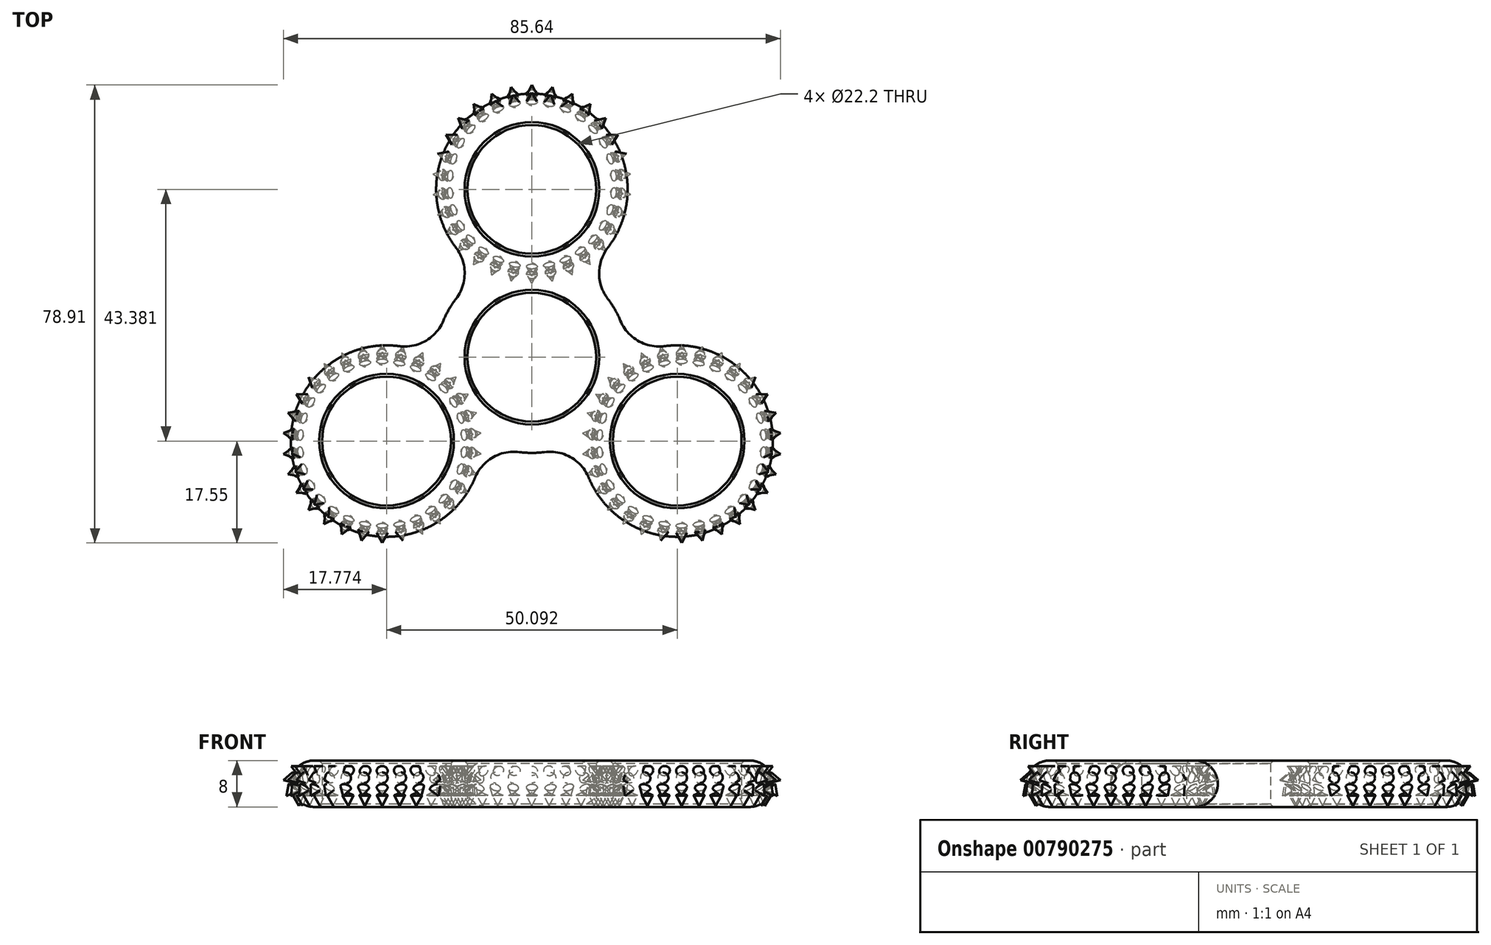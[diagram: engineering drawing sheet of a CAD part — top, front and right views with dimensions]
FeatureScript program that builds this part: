
annotation { "Feature Type Name" : "Feature", "Feature Type Description" : "" }
export const myFeature = defineFeature(function(context is Context, id is Id, definition is map)
    precondition{}
    {
        {
            var Q0;
            Q0=qCreatedBy(makeId("Top.planeOp"),FACE);
            var sketch = newSketch(context, id + "F0", { "sketchPlane" : qUnion([Q0])});
            skCircle(sketch, "E0", {"center": v(0, 0) * mm, "radius": 11.1 * mm});
            skCircle(sketch, "E1", {"center": v(0, 0) * mm, "radius": 16.5 * mm});
            skCircle(sketch, "E2", {"center": v(0, 28.92) * mm, "radius": 16.5 * mm});
            skCircle(sketch, "E3", {"center": v(0, 28.92) * mm, "radius": 11.1 * mm});
            skCircle(sketch, "E4.1.0", {"center": v(-25.05, -14.46) * mm, "radius": 16.5 * mm});
            skCircle(sketch, "E4.1.1", {"center": v(-25.05, -14.46) * mm, "radius": 11.1 * mm});
            skCircle(sketch, "E4.2.0", {"center": v(25.05, -14.46) * mm, "radius": 16.5 * mm});
            skCircle(sketch, "E4.2.1", {"center": v(25.05, -14.46) * mm, "radius": 11.1 * mm});
            skSolve(sketch);
        }
        {
            var Q0;
            Q0=makeQuery(id+"F0.imprint","IMPRINT",FACE,{"disambiguationData":[TD([[makeQuery(id+"F0.imprint","IMPRINT",EDGE,{"derivedFrom":sQuery(id+"F0.wireOp",EDGE,"E4.1.1")}),-1.0]])]});
            var Q1;
            Q1=makeQuery(id+"F0.imprint","IMPRINT",FACE,{"disambiguationData":[TD([[makeQuery(id+"F0.imprint","IMPRINT",EDGE,{"derivedFrom":sQuery(id+"F0.wireOp",EDGE,"E0")}),-1.0]])]});
            var Q2;
            Q2=makeQuery(id+"F0.imprint","IMPRINT",FACE,{"disambiguationData":[TD([[makeQuery(id+"F0.imprint","IMPRINT",EDGE,{"derivedFrom":sQuery(id+"F0.wireOp",EDGE,"E3")}),-1.0]])]});
            var Q3;
            {var subQ0=sQuery(id+"F0.wireOp",EDGE,"E2");var subQ1=sQuery(id+"F0.wireOp",EDGE,"E1");var subQ2=makeQuery(id+"F0.imprint","INTERSECT",VERTEX,{"disambiguationData":[OD(0.0)],"derivedFrom":[subQ1,subQ0]});Q3=makeQuery(id+"F0.imprint","IMPRINT",FACE,{"disambiguationData":[TD([[makeQuery(id+"F0.imprint","IMPRINT",EDGE,{"disambiguationData":[TD([[subQ2,1.0]])],"derivedFrom":subQ1}),1.0]])]});}
            var Q4;
            {var subQ0=sQuery(id+"F0.wireOp",EDGE,"E4.1.0");var subQ1=sQuery(id+"F0.wireOp",EDGE,"E1");var subQ2=makeQuery(id+"F0.imprint","INTERSECT",VERTEX,{"disambiguationData":[OD(0.0)],"derivedFrom":[subQ1,subQ0]});Q4=makeQuery(id+"F0.imprint","IMPRINT",FACE,{"disambiguationData":[TD([[makeQuery(id+"F0.imprint","IMPRINT",EDGE,{"disambiguationData":[TD([[subQ2,-1.0]])],"derivedFrom":subQ1}),1.0]])]});}
            var Q5;
            {var subQ0=sQuery(id+"F0.wireOp",EDGE,"E4.2.0");var subQ1=sQuery(id+"F0.wireOp",EDGE,"E1");var subQ2=makeQuery(id+"F0.imprint","INTERSECT",VERTEX,{"disambiguationData":[OD(0.0)],"derivedFrom":[subQ1,subQ0]});Q5=makeQuery(id+"F0.imprint","IMPRINT",FACE,{"disambiguationData":[TD([[makeQuery(id+"F0.imprint","IMPRINT",EDGE,{"disambiguationData":[TD([[subQ2,-1.0]])],"derivedFrom":subQ1}),1.0]])]});}
            var Q6;
            Q6=makeQuery(id+"F0.imprint","IMPRINT",FACE,{"disambiguationData":[TD([[makeQuery(id+"F0.imprint","IMPRINT",EDGE,{"derivedFrom":sQuery(id+"F0.wireOp",EDGE,"E4.2.1")}),-1.0]])]});
            extrude(context, id + "F1", {"entities" : qUnion([Q0, Q1, Q2, Q3, Q4, Q5, Q6]), "depth" : 8 * mm, "offsetDistance" : 25 * mm});
        }
        {
            var Q0;
            {var subQ0=sQuery(id+"F0.wireOp",EDGE,"E2");var subQ1=sQuery(id+"F0.wireOp",EDGE,"E1");Q0=makeQuery(id+"F1.opExtrude","SWEPT_EDGE",EDGE,{"disambiguationData":[OSD([subQ1,subQ0]),TDD([makeQuery(id+"F0.imprint","INTERSECT",VERTEX,{"disambiguationData":[OD(0.0)],"derivedFrom":[subQ1,subQ0]})])]});}
            var Q1;
            {var subQ0=sQuery(id+"F0.wireOp",EDGE,"E4.1.0");var subQ1=sQuery(id+"F0.wireOp",EDGE,"E1");Q1=makeQuery(id+"F1.opExtrude","SWEPT_EDGE",EDGE,{"disambiguationData":[OSD([subQ1,subQ0]),TDD([makeQuery(id+"F0.imprint","INTERSECT",VERTEX,{"disambiguationData":[OD(0.0)],"derivedFrom":[subQ1,subQ0]})])]});}
            var Q2;
            {var subQ0=sQuery(id+"F0.wireOp",EDGE,"E4.1.0");var subQ1=sQuery(id+"F0.wireOp",EDGE,"E1");Q2=makeQuery(id+"F1.opExtrude","SWEPT_EDGE",EDGE,{"disambiguationData":[OSD([subQ1,subQ0]),TDD([makeQuery(id+"F0.imprint","INTERSECT",VERTEX,{"disambiguationData":[OD(1.0)],"derivedFrom":[subQ1,subQ0]})])]});}
            var Q3;
            {var subQ0=sQuery(id+"F0.wireOp",EDGE,"E4.2.0");var subQ1=sQuery(id+"F0.wireOp",EDGE,"E1");Q3=makeQuery(id+"F1.opExtrude","SWEPT_EDGE",EDGE,{"disambiguationData":[OSD([subQ1,subQ0]),TDD([makeQuery(id+"F0.imprint","INTERSECT",VERTEX,{"disambiguationData":[OD(0.0)],"derivedFrom":[subQ1,subQ0]})])]});}
            var Q4;
            {var subQ0=sQuery(id+"F0.wireOp",EDGE,"E2");var subQ1=sQuery(id+"F0.wireOp",EDGE,"E1");Q4=makeQuery(id+"F1.opExtrude","SWEPT_EDGE",EDGE,{"disambiguationData":[OSD([subQ1,subQ0]),TDD([makeQuery(id+"F0.imprint","INTERSECT",VERTEX,{"disambiguationData":[OD(1.0)],"derivedFrom":[subQ1,subQ0]})])]});}
            var Q5;
            {var subQ0=sQuery(id+"F0.wireOp",EDGE,"E4.2.0");var subQ1=sQuery(id+"F0.wireOp",EDGE,"E1");Q5=makeQuery(id+"F1.opExtrude","SWEPT_EDGE",EDGE,{"disambiguationData":[OSD([subQ1,subQ0]),TDD([makeQuery(id+"F0.imprint","INTERSECT",VERTEX,{"disambiguationData":[OD(1.0)],"derivedFrom":[subQ1,subQ0]})])]});}
            fillet(context, id + "F2", {"entities" : qUnion([Q0, Q1, Q2, Q3, Q4, Q5]), "radius" : 7.25 * mm, "tangentPropagation" : true, "allowEdgeOverflow" : false});
        }
        {
            var Q0;
            Q0=makeQuery(id+"F1.opExtrude","CAP_EDGE",EDGE,{"disambiguationData":[OSD([sQuery(id+"F0.wireOp",EDGE,"E4.1.0")])],"isStart":true});
            var Q1;
            Q1=makeQuery(id+"F1.opExtrude","CAP_EDGE",EDGE,{"disambiguationData":[OSD([sQuery(id+"F0.wireOp",EDGE,"E4.1.0")])],"isStart":false});
            fillet(context, id + "F3", {"entities" : qUnion([Q0, Q1]), "radius" : 4 * mm, "tangentPropagation" : true, "allowEdgeOverflow" : false});
        }
        {
            var Q0;
            Q0=qCreatedBy(makeId("Top.planeOp"),FACE);
            cPlane(context, id + "F4", {"entities" : qUnion([Q0]), "cplaneType" : CPlaneType.OFFSET, "offset" : 4 * mm, "width" : 150 * mm, "height" : 150 * mm});
        }
        {
            var Q0;
            Q0=qCreatedBy(id+"F4.planeOp",FACE);
            var sketch = newSketch(context, id + "F5", { "sketchPlane" : qUnion([Q0])});
            skCircle(sketch, "E5", {"center": v(0, 29.79) * mm, "radius": 16.55 * mm, "construction": true});
            skPoint(sketch, "E6", {"position": v(0, 46.34) * mm});
            skSolve(sketch);
        }
        {
            var Q0;
            Q0=qCreatedBy(makeId("Right.planeOp"),FACE);
            var sketch = newSketch(context, id + "F6", { "sketchPlane" : qUnion([Q0])});
            skLineSegment(sketch, "E7", {"start": v(43.55, 6) * mm, "end": v(45.58, 7.03) * mm});
            skLineSegment(sketch, "E8", {"start": v(45.58, 7.03) * mm, "end": v(44.38, 5.37) * mm});
            skLineSegment(sketch, "E9", {"start": v(44.38, 5.37) * mm, "end": v(43.55, 6) * mm});
            skSolve(sketch);
        }
        {
            var Q0;
            Q0=makeQuery(id+"F6.imprint","IMPRINT",FACE,{"disambiguationData":[TD([[makeQuery(id+"F6.imprint","IMPRINT",EDGE,{"derivedFrom":sQuery(id+"F6.wireOp",EDGE,"E7")}),-1.0]])]});
            var Q1;
            Q1=sQuery(id+"F6.wireOp",EDGE,"E7");
            revolve(context, id + "F7", {"surfaceOperationType" : NewSurfaceOperationType.NEW, "entities" : qUnion([Q0]), "axis" : qUnion([Q1]), "revolveType" : RevolveType.FULL});
        }
        {
            var Q0;
            Q0=qCreatedBy(id+"F4.planeOp",FACE);
            var sketch = newSketch(context, id + "F8", { "sketchPlane" : qUnion([Q0])});
            skLineSegment(sketch, "E10", {"start": v(-52.95, 42.91) * mm, "end": v(50.46, 42.91) * mm, "construction": true});
            skSolve(sketch);
        }
        {
            var Q0;
            Q0=makeQuery(id+"F7.opRevolve","SWEPT_BODY",BODY,{"disambiguationData":[OSD([sQuery(id+"F6.wireOp",EDGE,"E7"),sQuery(id+"F6.wireOp",EDGE,"RLVqaSlf-lc0r-w3OG-rFOS-OxLLSJ0IXL9I"),sQuery(id+"F6.wireOp",EDGE,"E8"),sQuery(id+"F6.wireOp",EDGE,"E9")])]});
            var Q1;
            Q1=sQuery(id+"F8.wireOp",EDGE,"E10");
            circularPattern(context, id + "F9", {"entities" : qUnion([Q0]), "axis" : qUnion([Q1]), "angle" : 120 * degree, "instanceCount" : 4, "oppositeDirection" : true, "equalSpace" : true});
        }
        {
            var Q0;
            Q0=makeQuery(id+"F9.opPattern","COPY",BODY,{"derivedFrom":makeQuery(id+"F7.opRevolve","SWEPT_BODY",BODY,{"disambiguationData":[OSD([sQuery(id+"F6.wireOp",EDGE,"E7"),sQuery(id+"F6.wireOp",EDGE,"RLVqaSlf-lc0r-w3OG-rFOS-OxLLSJ0IXL9I"),sQuery(id+"F6.wireOp",EDGE,"E8"),sQuery(id+"F6.wireOp",EDGE,"E9")])]}),"instanceName":"3"});
            var Q1;
            Q1=makeQuery(id+"F9.opPattern","COPY",BODY,{"derivedFrom":makeQuery(id+"F7.opRevolve","SWEPT_BODY",BODY,{"disambiguationData":[OSD([sQuery(id+"F6.wireOp",EDGE,"E7"),sQuery(id+"F6.wireOp",EDGE,"RLVqaSlf-lc0r-w3OG-rFOS-OxLLSJ0IXL9I"),sQuery(id+"F6.wireOp",EDGE,"E8"),sQuery(id+"F6.wireOp",EDGE,"E9")])]}),"instanceName":"2"});
            var Q2;
            Q2=makeQuery(id+"F9.opPattern","COPY",BODY,{"derivedFrom":makeQuery(id+"F7.opRevolve","SWEPT_BODY",BODY,{"disambiguationData":[OSD([sQuery(id+"F6.wireOp",EDGE,"E7"),sQuery(id+"F6.wireOp",EDGE,"RLVqaSlf-lc0r-w3OG-rFOS-OxLLSJ0IXL9I"),sQuery(id+"F6.wireOp",EDGE,"E8"),sQuery(id+"F6.wireOp",EDGE,"E9")])]}),"instanceName":"1"});
            var Q3;
            Q3=makeQuery(id+"F7.opRevolve","SWEPT_BODY",BODY,{"disambiguationData":[OSD([sQuery(id+"F6.wireOp",EDGE,"E7"),sQuery(id+"F6.wireOp",EDGE,"RLVqaSlf-lc0r-w3OG-rFOS-OxLLSJ0IXL9I"),sQuery(id+"F6.wireOp",EDGE,"E8"),sQuery(id+"F6.wireOp",EDGE,"E9")])]});
            var Q4;
            Q4=sQuery(id+"F5.wireOp",EDGE,"E5");
            circularPattern(context, id + "F10", {"entities" : qUnion([Q0, Q1, Q2, Q3]), "axis" : qUnion([Q4]), "angle" : 360 * degree, "instanceCount" : 30, "equalSpace" : true});
        }
        {
            var Q0;
            Q0=qCreatedBy(makeId("Right.planeOp"),FACE);
            var sketch = newSketch(context, id + "F11", { "sketchPlane" : qUnion([Q0])});
            skLineSegment(sketch, "E11", {"start": v(0, -37.59) * mm, "end": v(0, 50.22) * mm, "construction": true});
            skSolve(sketch);
        }
        {
            var Q0;
            Q0=makeQuery(id+"F10.opPattern","COPY",BODY,{"derivedFrom":makeQuery(id+"F9.opPattern","COPY",BODY,{"derivedFrom":makeQuery(id+"F7.opRevolve","SWEPT_BODY",BODY,{"disambiguationData":[OSD([sQuery(id+"F6.wireOp",EDGE,"E7"),sQuery(id+"F6.wireOp",EDGE,"RLVqaSlf-lc0r-w3OG-rFOS-OxLLSJ0IXL9I"),sQuery(id+"F6.wireOp",EDGE,"E8"),sQuery(id+"F6.wireOp",EDGE,"E9")])]}),"instanceName":"2"}),"instanceName":"1"});
            var Q1;
            Q1=makeQuery(id+"F10.opPattern","COPY",BODY,{"derivedFrom":makeQuery(id+"F7.opRevolve","SWEPT_BODY",BODY,{"disambiguationData":[OSD([sQuery(id+"F6.wireOp",EDGE,"E7"),sQuery(id+"F6.wireOp",EDGE,"RLVqaSlf-lc0r-w3OG-rFOS-OxLLSJ0IXL9I"),sQuery(id+"F6.wireOp",EDGE,"E8"),sQuery(id+"F6.wireOp",EDGE,"E9")])]}),"instanceName":"1"});
            var Q2;
            Q2=makeQuery(id+"F10.opPattern","COPY",BODY,{"derivedFrom":makeQuery(id+"F9.opPattern","COPY",BODY,{"derivedFrom":makeQuery(id+"F7.opRevolve","SWEPT_BODY",BODY,{"disambiguationData":[OSD([sQuery(id+"F6.wireOp",EDGE,"E7"),sQuery(id+"F6.wireOp",EDGE,"RLVqaSlf-lc0r-w3OG-rFOS-OxLLSJ0IXL9I"),sQuery(id+"F6.wireOp",EDGE,"E8"),sQuery(id+"F6.wireOp",EDGE,"E9")])]}),"instanceName":"1"}),"instanceName":"1"});
            var Q3;
            Q3=makeQuery(id+"F9.opPattern","COPY",BODY,{"derivedFrom":makeQuery(id+"F7.opRevolve","SWEPT_BODY",BODY,{"disambiguationData":[OSD([sQuery(id+"F6.wireOp",EDGE,"E7"),sQuery(id+"F6.wireOp",EDGE,"RLVqaSlf-lc0r-w3OG-rFOS-OxLLSJ0IXL9I"),sQuery(id+"F6.wireOp",EDGE,"E8"),sQuery(id+"F6.wireOp",EDGE,"E9")])]}),"instanceName":"1"});
            var Q4;
            Q4=makeQuery(id+"F9.opPattern","COPY",BODY,{"derivedFrom":makeQuery(id+"F7.opRevolve","SWEPT_BODY",BODY,{"disambiguationData":[OSD([sQuery(id+"F6.wireOp",EDGE,"E7"),sQuery(id+"F6.wireOp",EDGE,"RLVqaSlf-lc0r-w3OG-rFOS-OxLLSJ0IXL9I"),sQuery(id+"F6.wireOp",EDGE,"E8"),sQuery(id+"F6.wireOp",EDGE,"E9")])]}),"instanceName":"2"});
            var Q5;
            Q5=makeQuery(id+"F9.opPattern","COPY",BODY,{"derivedFrom":makeQuery(id+"F7.opRevolve","SWEPT_BODY",BODY,{"disambiguationData":[OSD([sQuery(id+"F6.wireOp",EDGE,"E7"),sQuery(id+"F6.wireOp",EDGE,"RLVqaSlf-lc0r-w3OG-rFOS-OxLLSJ0IXL9I"),sQuery(id+"F6.wireOp",EDGE,"E8"),sQuery(id+"F6.wireOp",EDGE,"E9")])]}),"instanceName":"3"});
            var Q6;
            Q6=makeQuery(id+"F10.opPattern","COPY",BODY,{"derivedFrom":makeQuery(id+"F9.opPattern","COPY",BODY,{"derivedFrom":makeQuery(id+"F7.opRevolve","SWEPT_BODY",BODY,{"disambiguationData":[OSD([sQuery(id+"F6.wireOp",EDGE,"E7"),sQuery(id+"F6.wireOp",EDGE,"RLVqaSlf-lc0r-w3OG-rFOS-OxLLSJ0IXL9I"),sQuery(id+"F6.wireOp",EDGE,"E8"),sQuery(id+"F6.wireOp",EDGE,"E9")])]}),"instanceName":"2"}),"instanceName":"2"});
            var Q7;
            Q7=makeQuery(id+"F10.opPattern","COPY",BODY,{"derivedFrom":makeQuery(id+"F9.opPattern","COPY",BODY,{"derivedFrom":makeQuery(id+"F7.opRevolve","SWEPT_BODY",BODY,{"disambiguationData":[OSD([sQuery(id+"F6.wireOp",EDGE,"E7"),sQuery(id+"F6.wireOp",EDGE,"RLVqaSlf-lc0r-w3OG-rFOS-OxLLSJ0IXL9I"),sQuery(id+"F6.wireOp",EDGE,"E8"),sQuery(id+"F6.wireOp",EDGE,"E9")])]}),"instanceName":"1"}),"instanceName":"2"});
            var Q8;
            Q8=makeQuery(id+"F10.opPattern","COPY",BODY,{"derivedFrom":makeQuery(id+"F9.opPattern","COPY",BODY,{"derivedFrom":makeQuery(id+"F7.opRevolve","SWEPT_BODY",BODY,{"disambiguationData":[OSD([sQuery(id+"F6.wireOp",EDGE,"E7"),sQuery(id+"F6.wireOp",EDGE,"RLVqaSlf-lc0r-w3OG-rFOS-OxLLSJ0IXL9I"),sQuery(id+"F6.wireOp",EDGE,"E8"),sQuery(id+"F6.wireOp",EDGE,"E9")])]}),"instanceName":"3"}),"instanceName":"2"});
            var Q9;
            Q9=makeQuery(id+"F10.opPattern","COPY",BODY,{"derivedFrom":makeQuery(id+"F7.opRevolve","SWEPT_BODY",BODY,{"disambiguationData":[OSD([sQuery(id+"F6.wireOp",EDGE,"E7"),sQuery(id+"F6.wireOp",EDGE,"RLVqaSlf-lc0r-w3OG-rFOS-OxLLSJ0IXL9I"),sQuery(id+"F6.wireOp",EDGE,"E8"),sQuery(id+"F6.wireOp",EDGE,"E9")])]}),"instanceName":"3"});
            var Q10;
            Q10=makeQuery(id+"F10.opPattern","COPY",BODY,{"derivedFrom":makeQuery(id+"F9.opPattern","COPY",BODY,{"derivedFrom":makeQuery(id+"F7.opRevolve","SWEPT_BODY",BODY,{"disambiguationData":[OSD([sQuery(id+"F6.wireOp",EDGE,"E7"),sQuery(id+"F6.wireOp",EDGE,"RLVqaSlf-lc0r-w3OG-rFOS-OxLLSJ0IXL9I"),sQuery(id+"F6.wireOp",EDGE,"E8"),sQuery(id+"F6.wireOp",EDGE,"E9")])]}),"instanceName":"1"}),"instanceName":"3"});
            var Q11;
            Q11=makeQuery(id+"F10.opPattern","COPY",BODY,{"derivedFrom":makeQuery(id+"F9.opPattern","COPY",BODY,{"derivedFrom":makeQuery(id+"F7.opRevolve","SWEPT_BODY",BODY,{"disambiguationData":[OSD([sQuery(id+"F6.wireOp",EDGE,"E7"),sQuery(id+"F6.wireOp",EDGE,"RLVqaSlf-lc0r-w3OG-rFOS-OxLLSJ0IXL9I"),sQuery(id+"F6.wireOp",EDGE,"E8"),sQuery(id+"F6.wireOp",EDGE,"E9")])]}),"instanceName":"2"}),"instanceName":"3"});
            var Q12;
            Q12=makeQuery(id+"F10.opPattern","COPY",BODY,{"derivedFrom":makeQuery(id+"F9.opPattern","COPY",BODY,{"derivedFrom":makeQuery(id+"F7.opRevolve","SWEPT_BODY",BODY,{"disambiguationData":[OSD([sQuery(id+"F6.wireOp",EDGE,"E7"),sQuery(id+"F6.wireOp",EDGE,"RLVqaSlf-lc0r-w3OG-rFOS-OxLLSJ0IXL9I"),sQuery(id+"F6.wireOp",EDGE,"E8"),sQuery(id+"F6.wireOp",EDGE,"E9")])]}),"instanceName":"3"}),"instanceName":"3"});
            var Q13;
            Q13=makeQuery(id+"F10.opPattern","COPY",BODY,{"derivedFrom":makeQuery(id+"F7.opRevolve","SWEPT_BODY",BODY,{"disambiguationData":[OSD([sQuery(id+"F6.wireOp",EDGE,"E7"),sQuery(id+"F6.wireOp",EDGE,"RLVqaSlf-lc0r-w3OG-rFOS-OxLLSJ0IXL9I"),sQuery(id+"F6.wireOp",EDGE,"E8"),sQuery(id+"F6.wireOp",EDGE,"E9")])]}),"instanceName":"4"});
            var Q14;
            Q14=makeQuery(id+"F10.opPattern","COPY",BODY,{"derivedFrom":makeQuery(id+"F9.opPattern","COPY",BODY,{"derivedFrom":makeQuery(id+"F7.opRevolve","SWEPT_BODY",BODY,{"disambiguationData":[OSD([sQuery(id+"F6.wireOp",EDGE,"E7"),sQuery(id+"F6.wireOp",EDGE,"RLVqaSlf-lc0r-w3OG-rFOS-OxLLSJ0IXL9I"),sQuery(id+"F6.wireOp",EDGE,"E8"),sQuery(id+"F6.wireOp",EDGE,"E9")])]}),"instanceName":"1"}),"instanceName":"4"});
            var Q15;
            Q15=makeQuery(id+"F10.opPattern","COPY",BODY,{"derivedFrom":makeQuery(id+"F9.opPattern","COPY",BODY,{"derivedFrom":makeQuery(id+"F7.opRevolve","SWEPT_BODY",BODY,{"disambiguationData":[OSD([sQuery(id+"F6.wireOp",EDGE,"E7"),sQuery(id+"F6.wireOp",EDGE,"RLVqaSlf-lc0r-w3OG-rFOS-OxLLSJ0IXL9I"),sQuery(id+"F6.wireOp",EDGE,"E8"),sQuery(id+"F6.wireOp",EDGE,"E9")])]}),"instanceName":"2"}),"instanceName":"4"});
            var Q16;
            Q16=makeQuery(id+"F10.opPattern","COPY",BODY,{"derivedFrom":makeQuery(id+"F9.opPattern","COPY",BODY,{"derivedFrom":makeQuery(id+"F7.opRevolve","SWEPT_BODY",BODY,{"disambiguationData":[OSD([sQuery(id+"F6.wireOp",EDGE,"E7"),sQuery(id+"F6.wireOp",EDGE,"RLVqaSlf-lc0r-w3OG-rFOS-OxLLSJ0IXL9I"),sQuery(id+"F6.wireOp",EDGE,"E8"),sQuery(id+"F6.wireOp",EDGE,"E9")])]}),"instanceName":"3"}),"instanceName":"4"});
            var Q17;
            Q17=makeQuery(id+"F10.opPattern","COPY",BODY,{"derivedFrom":makeQuery(id+"F7.opRevolve","SWEPT_BODY",BODY,{"disambiguationData":[OSD([sQuery(id+"F6.wireOp",EDGE,"E7"),sQuery(id+"F6.wireOp",EDGE,"RLVqaSlf-lc0r-w3OG-rFOS-OxLLSJ0IXL9I"),sQuery(id+"F6.wireOp",EDGE,"E8"),sQuery(id+"F6.wireOp",EDGE,"E9")])]}),"instanceName":"5"});
            var Q18;
            Q18=makeQuery(id+"F10.opPattern","COPY",BODY,{"derivedFrom":makeQuery(id+"F9.opPattern","COPY",BODY,{"derivedFrom":makeQuery(id+"F7.opRevolve","SWEPT_BODY",BODY,{"disambiguationData":[OSD([sQuery(id+"F6.wireOp",EDGE,"E7"),sQuery(id+"F6.wireOp",EDGE,"RLVqaSlf-lc0r-w3OG-rFOS-OxLLSJ0IXL9I"),sQuery(id+"F6.wireOp",EDGE,"E8"),sQuery(id+"F6.wireOp",EDGE,"E9")])]}),"instanceName":"1"}),"instanceName":"5"});
            var Q19;
            Q19=makeQuery(id+"F10.opPattern","COPY",BODY,{"derivedFrom":makeQuery(id+"F9.opPattern","COPY",BODY,{"derivedFrom":makeQuery(id+"F7.opRevolve","SWEPT_BODY",BODY,{"disambiguationData":[OSD([sQuery(id+"F6.wireOp",EDGE,"E7"),sQuery(id+"F6.wireOp",EDGE,"RLVqaSlf-lc0r-w3OG-rFOS-OxLLSJ0IXL9I"),sQuery(id+"F6.wireOp",EDGE,"E8"),sQuery(id+"F6.wireOp",EDGE,"E9")])]}),"instanceName":"2"}),"instanceName":"5"});
            var Q20;
            Q20=makeQuery(id+"F10.opPattern","COPY",BODY,{"derivedFrom":makeQuery(id+"F9.opPattern","COPY",BODY,{"derivedFrom":makeQuery(id+"F7.opRevolve","SWEPT_BODY",BODY,{"disambiguationData":[OSD([sQuery(id+"F6.wireOp",EDGE,"E7"),sQuery(id+"F6.wireOp",EDGE,"RLVqaSlf-lc0r-w3OG-rFOS-OxLLSJ0IXL9I"),sQuery(id+"F6.wireOp",EDGE,"E8"),sQuery(id+"F6.wireOp",EDGE,"E9")])]}),"instanceName":"3"}),"instanceName":"5"});
            var Q21;
            Q21=makeQuery(id+"F10.opPattern","COPY",BODY,{"derivedFrom":makeQuery(id+"F7.opRevolve","SWEPT_BODY",BODY,{"disambiguationData":[OSD([sQuery(id+"F6.wireOp",EDGE,"E7"),sQuery(id+"F6.wireOp",EDGE,"RLVqaSlf-lc0r-w3OG-rFOS-OxLLSJ0IXL9I"),sQuery(id+"F6.wireOp",EDGE,"E8"),sQuery(id+"F6.wireOp",EDGE,"E9")])]}),"instanceName":"6"});
            var Q22;
            Q22=makeQuery(id+"F10.opPattern","COPY",BODY,{"derivedFrom":makeQuery(id+"F9.opPattern","COPY",BODY,{"derivedFrom":makeQuery(id+"F7.opRevolve","SWEPT_BODY",BODY,{"disambiguationData":[OSD([sQuery(id+"F6.wireOp",EDGE,"E7"),sQuery(id+"F6.wireOp",EDGE,"RLVqaSlf-lc0r-w3OG-rFOS-OxLLSJ0IXL9I"),sQuery(id+"F6.wireOp",EDGE,"E8"),sQuery(id+"F6.wireOp",EDGE,"E9")])]}),"instanceName":"1"}),"instanceName":"6"});
            var Q23;
            Q23=makeQuery(id+"F10.opPattern","COPY",BODY,{"derivedFrom":makeQuery(id+"F9.opPattern","COPY",BODY,{"derivedFrom":makeQuery(id+"F7.opRevolve","SWEPT_BODY",BODY,{"disambiguationData":[OSD([sQuery(id+"F6.wireOp",EDGE,"E7"),sQuery(id+"F6.wireOp",EDGE,"RLVqaSlf-lc0r-w3OG-rFOS-OxLLSJ0IXL9I"),sQuery(id+"F6.wireOp",EDGE,"E8"),sQuery(id+"F6.wireOp",EDGE,"E9")])]}),"instanceName":"2"}),"instanceName":"6"});
            var Q24;
            Q24=makeQuery(id+"F10.opPattern","COPY",BODY,{"derivedFrom":makeQuery(id+"F9.opPattern","COPY",BODY,{"derivedFrom":makeQuery(id+"F7.opRevolve","SWEPT_BODY",BODY,{"disambiguationData":[OSD([sQuery(id+"F6.wireOp",EDGE,"E7"),sQuery(id+"F6.wireOp",EDGE,"RLVqaSlf-lc0r-w3OG-rFOS-OxLLSJ0IXL9I"),sQuery(id+"F6.wireOp",EDGE,"E8"),sQuery(id+"F6.wireOp",EDGE,"E9")])]}),"instanceName":"3"}),"instanceName":"6"});
            var Q25;
            Q25=makeQuery(id+"F10.opPattern","COPY",BODY,{"derivedFrom":makeQuery(id+"F9.opPattern","COPY",BODY,{"derivedFrom":makeQuery(id+"F7.opRevolve","SWEPT_BODY",BODY,{"disambiguationData":[OSD([sQuery(id+"F6.wireOp",EDGE,"E7"),sQuery(id+"F6.wireOp",EDGE,"RLVqaSlf-lc0r-w3OG-rFOS-OxLLSJ0IXL9I"),sQuery(id+"F6.wireOp",EDGE,"E8"),sQuery(id+"F6.wireOp",EDGE,"E9")])]}),"instanceName":"1"}),"instanceName":"7"});
            var Q26;
            Q26=makeQuery(id+"F10.opPattern","COPY",BODY,{"derivedFrom":makeQuery(id+"F9.opPattern","COPY",BODY,{"derivedFrom":makeQuery(id+"F7.opRevolve","SWEPT_BODY",BODY,{"disambiguationData":[OSD([sQuery(id+"F6.wireOp",EDGE,"E7"),sQuery(id+"F6.wireOp",EDGE,"RLVqaSlf-lc0r-w3OG-rFOS-OxLLSJ0IXL9I"),sQuery(id+"F6.wireOp",EDGE,"E8"),sQuery(id+"F6.wireOp",EDGE,"E9")])]}),"instanceName":"2"}),"instanceName":"7"});
            var Q27;
            Q27=makeQuery(id+"F10.opPattern","COPY",BODY,{"derivedFrom":makeQuery(id+"F9.opPattern","COPY",BODY,{"derivedFrom":makeQuery(id+"F7.opRevolve","SWEPT_BODY",BODY,{"disambiguationData":[OSD([sQuery(id+"F6.wireOp",EDGE,"E7"),sQuery(id+"F6.wireOp",EDGE,"RLVqaSlf-lc0r-w3OG-rFOS-OxLLSJ0IXL9I"),sQuery(id+"F6.wireOp",EDGE,"E8"),sQuery(id+"F6.wireOp",EDGE,"E9")])]}),"instanceName":"3"}),"instanceName":"7"});
            var Q28;
            Q28=makeQuery(id+"F10.opPattern","COPY",BODY,{"derivedFrom":makeQuery(id+"F9.opPattern","COPY",BODY,{"derivedFrom":makeQuery(id+"F7.opRevolve","SWEPT_BODY",BODY,{"disambiguationData":[OSD([sQuery(id+"F6.wireOp",EDGE,"E7"),sQuery(id+"F6.wireOp",EDGE,"RLVqaSlf-lc0r-w3OG-rFOS-OxLLSJ0IXL9I"),sQuery(id+"F6.wireOp",EDGE,"E8"),sQuery(id+"F6.wireOp",EDGE,"E9")])]}),"instanceName":"1"}),"instanceName":"8"});
            var Q29;
            Q29=makeQuery(id+"F10.opPattern","COPY",BODY,{"derivedFrom":makeQuery(id+"F9.opPattern","COPY",BODY,{"derivedFrom":makeQuery(id+"F7.opRevolve","SWEPT_BODY",BODY,{"disambiguationData":[OSD([sQuery(id+"F6.wireOp",EDGE,"E7"),sQuery(id+"F6.wireOp",EDGE,"RLVqaSlf-lc0r-w3OG-rFOS-OxLLSJ0IXL9I"),sQuery(id+"F6.wireOp",EDGE,"E8"),sQuery(id+"F6.wireOp",EDGE,"E9")])]}),"instanceName":"2"}),"instanceName":"8"});
            var Q30;
            Q30=makeQuery(id+"F10.opPattern","COPY",BODY,{"derivedFrom":makeQuery(id+"F9.opPattern","COPY",BODY,{"derivedFrom":makeQuery(id+"F7.opRevolve","SWEPT_BODY",BODY,{"disambiguationData":[OSD([sQuery(id+"F6.wireOp",EDGE,"E7"),sQuery(id+"F6.wireOp",EDGE,"RLVqaSlf-lc0r-w3OG-rFOS-OxLLSJ0IXL9I"),sQuery(id+"F6.wireOp",EDGE,"E8"),sQuery(id+"F6.wireOp",EDGE,"E9")])]}),"instanceName":"3"}),"instanceName":"8"});
            var Q31;
            Q31=makeQuery(id+"F10.opPattern","COPY",BODY,{"derivedFrom":makeQuery(id+"F9.opPattern","COPY",BODY,{"derivedFrom":makeQuery(id+"F7.opRevolve","SWEPT_BODY",BODY,{"disambiguationData":[OSD([sQuery(id+"F6.wireOp",EDGE,"E7"),sQuery(id+"F6.wireOp",EDGE,"RLVqaSlf-lc0r-w3OG-rFOS-OxLLSJ0IXL9I"),sQuery(id+"F6.wireOp",EDGE,"E8"),sQuery(id+"F6.wireOp",EDGE,"E9")])]}),"instanceName":"1"}),"instanceName":"9"});
            var Q32;
            Q32=makeQuery(id+"F10.opPattern","COPY",BODY,{"derivedFrom":makeQuery(id+"F9.opPattern","COPY",BODY,{"derivedFrom":makeQuery(id+"F7.opRevolve","SWEPT_BODY",BODY,{"disambiguationData":[OSD([sQuery(id+"F6.wireOp",EDGE,"E7"),sQuery(id+"F6.wireOp",EDGE,"RLVqaSlf-lc0r-w3OG-rFOS-OxLLSJ0IXL9I"),sQuery(id+"F6.wireOp",EDGE,"E8"),sQuery(id+"F6.wireOp",EDGE,"E9")])]}),"instanceName":"2"}),"instanceName":"9"});
            var Q33;
            Q33=makeQuery(id+"F10.opPattern","COPY",BODY,{"derivedFrom":makeQuery(id+"F9.opPattern","COPY",BODY,{"derivedFrom":makeQuery(id+"F7.opRevolve","SWEPT_BODY",BODY,{"disambiguationData":[OSD([sQuery(id+"F6.wireOp",EDGE,"E7"),sQuery(id+"F6.wireOp",EDGE,"RLVqaSlf-lc0r-w3OG-rFOS-OxLLSJ0IXL9I"),sQuery(id+"F6.wireOp",EDGE,"E8"),sQuery(id+"F6.wireOp",EDGE,"E9")])]}),"instanceName":"3"}),"instanceName":"9"});
            var Q34;
            Q34=makeQuery(id+"F10.opPattern","COPY",BODY,{"derivedFrom":makeQuery(id+"F9.opPattern","COPY",BODY,{"derivedFrom":makeQuery(id+"F7.opRevolve","SWEPT_BODY",BODY,{"disambiguationData":[OSD([sQuery(id+"F6.wireOp",EDGE,"E7"),sQuery(id+"F6.wireOp",EDGE,"RLVqaSlf-lc0r-w3OG-rFOS-OxLLSJ0IXL9I"),sQuery(id+"F6.wireOp",EDGE,"E8"),sQuery(id+"F6.wireOp",EDGE,"E9")])]}),"instanceName":"1"}),"instanceName":"10"});
            var Q35;
            Q35=makeQuery(id+"F10.opPattern","COPY",BODY,{"derivedFrom":makeQuery(id+"F9.opPattern","COPY",BODY,{"derivedFrom":makeQuery(id+"F7.opRevolve","SWEPT_BODY",BODY,{"disambiguationData":[OSD([sQuery(id+"F6.wireOp",EDGE,"E7"),sQuery(id+"F6.wireOp",EDGE,"RLVqaSlf-lc0r-w3OG-rFOS-OxLLSJ0IXL9I"),sQuery(id+"F6.wireOp",EDGE,"E8"),sQuery(id+"F6.wireOp",EDGE,"E9")])]}),"instanceName":"2"}),"instanceName":"10"});
            var Q36;
            Q36=makeQuery(id+"F10.opPattern","COPY",BODY,{"derivedFrom":makeQuery(id+"F9.opPattern","COPY",BODY,{"derivedFrom":makeQuery(id+"F7.opRevolve","SWEPT_BODY",BODY,{"disambiguationData":[OSD([sQuery(id+"F6.wireOp",EDGE,"E7"),sQuery(id+"F6.wireOp",EDGE,"RLVqaSlf-lc0r-w3OG-rFOS-OxLLSJ0IXL9I"),sQuery(id+"F6.wireOp",EDGE,"E8"),sQuery(id+"F6.wireOp",EDGE,"E9")])]}),"instanceName":"3"}),"instanceName":"10"});
            var Q37;
            Q37=makeQuery(id+"F10.opPattern","COPY",BODY,{"derivedFrom":makeQuery(id+"F9.opPattern","COPY",BODY,{"derivedFrom":makeQuery(id+"F7.opRevolve","SWEPT_BODY",BODY,{"disambiguationData":[OSD([sQuery(id+"F6.wireOp",EDGE,"E7"),sQuery(id+"F6.wireOp",EDGE,"RLVqaSlf-lc0r-w3OG-rFOS-OxLLSJ0IXL9I"),sQuery(id+"F6.wireOp",EDGE,"E8"),sQuery(id+"F6.wireOp",EDGE,"E9")])]}),"instanceName":"1"}),"instanceName":"11"});
            var Q38;
            Q38=makeQuery(id+"F10.opPattern","COPY",BODY,{"derivedFrom":makeQuery(id+"F9.opPattern","COPY",BODY,{"derivedFrom":makeQuery(id+"F7.opRevolve","SWEPT_BODY",BODY,{"disambiguationData":[OSD([sQuery(id+"F6.wireOp",EDGE,"E7"),sQuery(id+"F6.wireOp",EDGE,"RLVqaSlf-lc0r-w3OG-rFOS-OxLLSJ0IXL9I"),sQuery(id+"F6.wireOp",EDGE,"E8"),sQuery(id+"F6.wireOp",EDGE,"E9")])]}),"instanceName":"2"}),"instanceName":"11"});
            var Q39;
            Q39=makeQuery(id+"F10.opPattern","COPY",BODY,{"derivedFrom":makeQuery(id+"F9.opPattern","COPY",BODY,{"derivedFrom":makeQuery(id+"F7.opRevolve","SWEPT_BODY",BODY,{"disambiguationData":[OSD([sQuery(id+"F6.wireOp",EDGE,"E7"),sQuery(id+"F6.wireOp",EDGE,"RLVqaSlf-lc0r-w3OG-rFOS-OxLLSJ0IXL9I"),sQuery(id+"F6.wireOp",EDGE,"E8"),sQuery(id+"F6.wireOp",EDGE,"E9")])]}),"instanceName":"3"}),"instanceName":"11"});
            var Q40;
            Q40=makeQuery(id+"F10.opPattern","COPY",BODY,{"derivedFrom":makeQuery(id+"F9.opPattern","COPY",BODY,{"derivedFrom":makeQuery(id+"F7.opRevolve","SWEPT_BODY",BODY,{"disambiguationData":[OSD([sQuery(id+"F6.wireOp",EDGE,"E7"),sQuery(id+"F6.wireOp",EDGE,"RLVqaSlf-lc0r-w3OG-rFOS-OxLLSJ0IXL9I"),sQuery(id+"F6.wireOp",EDGE,"E8"),sQuery(id+"F6.wireOp",EDGE,"E9")])]}),"instanceName":"3"}),"instanceName":"12"});
            var Q41;
            Q41=makeQuery(id+"F10.opPattern","COPY",BODY,{"derivedFrom":makeQuery(id+"F9.opPattern","COPY",BODY,{"derivedFrom":makeQuery(id+"F7.opRevolve","SWEPT_BODY",BODY,{"disambiguationData":[OSD([sQuery(id+"F6.wireOp",EDGE,"E7"),sQuery(id+"F6.wireOp",EDGE,"RLVqaSlf-lc0r-w3OG-rFOS-OxLLSJ0IXL9I"),sQuery(id+"F6.wireOp",EDGE,"E8"),sQuery(id+"F6.wireOp",EDGE,"E9")])]}),"instanceName":"3"}),"instanceName":"13"});
            var Q42;
            Q42=makeQuery(id+"F10.opPattern","COPY",BODY,{"derivedFrom":makeQuery(id+"F9.opPattern","COPY",BODY,{"derivedFrom":makeQuery(id+"F7.opRevolve","SWEPT_BODY",BODY,{"disambiguationData":[OSD([sQuery(id+"F6.wireOp",EDGE,"E7"),sQuery(id+"F6.wireOp",EDGE,"RLVqaSlf-lc0r-w3OG-rFOS-OxLLSJ0IXL9I"),sQuery(id+"F6.wireOp",EDGE,"E8"),sQuery(id+"F6.wireOp",EDGE,"E9")])]}),"instanceName":"3"}),"instanceName":"14"});
            var Q43;
            Q43=makeQuery(id+"F10.opPattern","COPY",BODY,{"derivedFrom":makeQuery(id+"F9.opPattern","COPY",BODY,{"derivedFrom":makeQuery(id+"F7.opRevolve","SWEPT_BODY",BODY,{"disambiguationData":[OSD([sQuery(id+"F6.wireOp",EDGE,"E7"),sQuery(id+"F6.wireOp",EDGE,"RLVqaSlf-lc0r-w3OG-rFOS-OxLLSJ0IXL9I"),sQuery(id+"F6.wireOp",EDGE,"E8"),sQuery(id+"F6.wireOp",EDGE,"E9")])]}),"instanceName":"3"}),"instanceName":"15"});
            var Q44;
            Q44=makeQuery(id+"F10.opPattern","COPY",BODY,{"derivedFrom":makeQuery(id+"F9.opPattern","COPY",BODY,{"derivedFrom":makeQuery(id+"F7.opRevolve","SWEPT_BODY",BODY,{"disambiguationData":[OSD([sQuery(id+"F6.wireOp",EDGE,"E7"),sQuery(id+"F6.wireOp",EDGE,"RLVqaSlf-lc0r-w3OG-rFOS-OxLLSJ0IXL9I"),sQuery(id+"F6.wireOp",EDGE,"E8"),sQuery(id+"F6.wireOp",EDGE,"E9")])]}),"instanceName":"3"}),"instanceName":"16"});
            var Q45;
            Q45=makeQuery(id+"F10.opPattern","COPY",BODY,{"derivedFrom":makeQuery(id+"F9.opPattern","COPY",BODY,{"derivedFrom":makeQuery(id+"F7.opRevolve","SWEPT_BODY",BODY,{"disambiguationData":[OSD([sQuery(id+"F6.wireOp",EDGE,"E7"),sQuery(id+"F6.wireOp",EDGE,"RLVqaSlf-lc0r-w3OG-rFOS-OxLLSJ0IXL9I"),sQuery(id+"F6.wireOp",EDGE,"E8"),sQuery(id+"F6.wireOp",EDGE,"E9")])]}),"instanceName":"3"}),"instanceName":"17"});
            var Q46;
            Q46=makeQuery(id+"F10.opPattern","COPY",BODY,{"derivedFrom":makeQuery(id+"F9.opPattern","COPY",BODY,{"derivedFrom":makeQuery(id+"F7.opRevolve","SWEPT_BODY",BODY,{"disambiguationData":[OSD([sQuery(id+"F6.wireOp",EDGE,"E7"),sQuery(id+"F6.wireOp",EDGE,"RLVqaSlf-lc0r-w3OG-rFOS-OxLLSJ0IXL9I"),sQuery(id+"F6.wireOp",EDGE,"E8"),sQuery(id+"F6.wireOp",EDGE,"E9")])]}),"instanceName":"3"}),"instanceName":"18"});
            var Q47;
            Q47=makeQuery(id+"F10.opPattern","COPY",BODY,{"derivedFrom":makeQuery(id+"F9.opPattern","COPY",BODY,{"derivedFrom":makeQuery(id+"F7.opRevolve","SWEPT_BODY",BODY,{"disambiguationData":[OSD([sQuery(id+"F6.wireOp",EDGE,"E7"),sQuery(id+"F6.wireOp",EDGE,"RLVqaSlf-lc0r-w3OG-rFOS-OxLLSJ0IXL9I"),sQuery(id+"F6.wireOp",EDGE,"E8"),sQuery(id+"F6.wireOp",EDGE,"E9")])]}),"instanceName":"2"}),"instanceName":"19"});
            var Q48;
            Q48=makeQuery(id+"F10.opPattern","COPY",BODY,{"derivedFrom":makeQuery(id+"F9.opPattern","COPY",BODY,{"derivedFrom":makeQuery(id+"F7.opRevolve","SWEPT_BODY",BODY,{"disambiguationData":[OSD([sQuery(id+"F6.wireOp",EDGE,"E7"),sQuery(id+"F6.wireOp",EDGE,"RLVqaSlf-lc0r-w3OG-rFOS-OxLLSJ0IXL9I"),sQuery(id+"F6.wireOp",EDGE,"E8"),sQuery(id+"F6.wireOp",EDGE,"E9")])]}),"instanceName":"3"}),"instanceName":"19"});
            var Q49;
            Q49=makeQuery(id+"F10.opPattern","COPY",BODY,{"derivedFrom":makeQuery(id+"F9.opPattern","COPY",BODY,{"derivedFrom":makeQuery(id+"F7.opRevolve","SWEPT_BODY",BODY,{"disambiguationData":[OSD([sQuery(id+"F6.wireOp",EDGE,"E7"),sQuery(id+"F6.wireOp",EDGE,"RLVqaSlf-lc0r-w3OG-rFOS-OxLLSJ0IXL9I"),sQuery(id+"F6.wireOp",EDGE,"E8"),sQuery(id+"F6.wireOp",EDGE,"E9")])]}),"instanceName":"2"}),"instanceName":"20"});
            var Q50;
            Q50=makeQuery(id+"F10.opPattern","COPY",BODY,{"derivedFrom":makeQuery(id+"F9.opPattern","COPY",BODY,{"derivedFrom":makeQuery(id+"F7.opRevolve","SWEPT_BODY",BODY,{"disambiguationData":[OSD([sQuery(id+"F6.wireOp",EDGE,"E7"),sQuery(id+"F6.wireOp",EDGE,"RLVqaSlf-lc0r-w3OG-rFOS-OxLLSJ0IXL9I"),sQuery(id+"F6.wireOp",EDGE,"E8"),sQuery(id+"F6.wireOp",EDGE,"E9")])]}),"instanceName":"3"}),"instanceName":"20"});
            var Q51;
            Q51=makeQuery(id+"F10.opPattern","COPY",BODY,{"derivedFrom":makeQuery(id+"F9.opPattern","COPY",BODY,{"derivedFrom":makeQuery(id+"F7.opRevolve","SWEPT_BODY",BODY,{"disambiguationData":[OSD([sQuery(id+"F6.wireOp",EDGE,"E7"),sQuery(id+"F6.wireOp",EDGE,"RLVqaSlf-lc0r-w3OG-rFOS-OxLLSJ0IXL9I"),sQuery(id+"F6.wireOp",EDGE,"E8"),sQuery(id+"F6.wireOp",EDGE,"E9")])]}),"instanceName":"1"}),"instanceName":"21"});
            var Q52;
            Q52=makeQuery(id+"F10.opPattern","COPY",BODY,{"derivedFrom":makeQuery(id+"F9.opPattern","COPY",BODY,{"derivedFrom":makeQuery(id+"F7.opRevolve","SWEPT_BODY",BODY,{"disambiguationData":[OSD([sQuery(id+"F6.wireOp",EDGE,"E7"),sQuery(id+"F6.wireOp",EDGE,"RLVqaSlf-lc0r-w3OG-rFOS-OxLLSJ0IXL9I"),sQuery(id+"F6.wireOp",EDGE,"E8"),sQuery(id+"F6.wireOp",EDGE,"E9")])]}),"instanceName":"2"}),"instanceName":"21"});
            var Q53;
            Q53=makeQuery(id+"F10.opPattern","COPY",BODY,{"derivedFrom":makeQuery(id+"F9.opPattern","COPY",BODY,{"derivedFrom":makeQuery(id+"F7.opRevolve","SWEPT_BODY",BODY,{"disambiguationData":[OSD([sQuery(id+"F6.wireOp",EDGE,"E7"),sQuery(id+"F6.wireOp",EDGE,"RLVqaSlf-lc0r-w3OG-rFOS-OxLLSJ0IXL9I"),sQuery(id+"F6.wireOp",EDGE,"E8"),sQuery(id+"F6.wireOp",EDGE,"E9")])]}),"instanceName":"3"}),"instanceName":"21"});
            var Q54;
            Q54=makeQuery(id+"F10.opPattern","COPY",BODY,{"derivedFrom":makeQuery(id+"F9.opPattern","COPY",BODY,{"derivedFrom":makeQuery(id+"F7.opRevolve","SWEPT_BODY",BODY,{"disambiguationData":[OSD([sQuery(id+"F6.wireOp",EDGE,"E7"),sQuery(id+"F6.wireOp",EDGE,"RLVqaSlf-lc0r-w3OG-rFOS-OxLLSJ0IXL9I"),sQuery(id+"F6.wireOp",EDGE,"E8"),sQuery(id+"F6.wireOp",EDGE,"E9")])]}),"instanceName":"1"}),"instanceName":"22"});
            var Q55;
            Q55=makeQuery(id+"F10.opPattern","COPY",BODY,{"derivedFrom":makeQuery(id+"F9.opPattern","COPY",BODY,{"derivedFrom":makeQuery(id+"F7.opRevolve","SWEPT_BODY",BODY,{"disambiguationData":[OSD([sQuery(id+"F6.wireOp",EDGE,"E7"),sQuery(id+"F6.wireOp",EDGE,"RLVqaSlf-lc0r-w3OG-rFOS-OxLLSJ0IXL9I"),sQuery(id+"F6.wireOp",EDGE,"E8"),sQuery(id+"F6.wireOp",EDGE,"E9")])]}),"instanceName":"2"}),"instanceName":"22"});
            var Q56;
            Q56=makeQuery(id+"F10.opPattern","COPY",BODY,{"derivedFrom":makeQuery(id+"F9.opPattern","COPY",BODY,{"derivedFrom":makeQuery(id+"F7.opRevolve","SWEPT_BODY",BODY,{"disambiguationData":[OSD([sQuery(id+"F6.wireOp",EDGE,"E7"),sQuery(id+"F6.wireOp",EDGE,"RLVqaSlf-lc0r-w3OG-rFOS-OxLLSJ0IXL9I"),sQuery(id+"F6.wireOp",EDGE,"E8"),sQuery(id+"F6.wireOp",EDGE,"E9")])]}),"instanceName":"3"}),"instanceName":"22"});
            var Q57;
            Q57=makeQuery(id+"F10.opPattern","COPY",BODY,{"derivedFrom":makeQuery(id+"F9.opPattern","COPY",BODY,{"derivedFrom":makeQuery(id+"F7.opRevolve","SWEPT_BODY",BODY,{"disambiguationData":[OSD([sQuery(id+"F6.wireOp",EDGE,"E7"),sQuery(id+"F6.wireOp",EDGE,"RLVqaSlf-lc0r-w3OG-rFOS-OxLLSJ0IXL9I"),sQuery(id+"F6.wireOp",EDGE,"E8"),sQuery(id+"F6.wireOp",EDGE,"E9")])]}),"instanceName":"1"}),"instanceName":"23"});
            var Q58;
            Q58=makeQuery(id+"F10.opPattern","COPY",BODY,{"derivedFrom":makeQuery(id+"F9.opPattern","COPY",BODY,{"derivedFrom":makeQuery(id+"F7.opRevolve","SWEPT_BODY",BODY,{"disambiguationData":[OSD([sQuery(id+"F6.wireOp",EDGE,"E7"),sQuery(id+"F6.wireOp",EDGE,"RLVqaSlf-lc0r-w3OG-rFOS-OxLLSJ0IXL9I"),sQuery(id+"F6.wireOp",EDGE,"E8"),sQuery(id+"F6.wireOp",EDGE,"E9")])]}),"instanceName":"2"}),"instanceName":"23"});
            var Q59;
            Q59=makeQuery(id+"F10.opPattern","COPY",BODY,{"derivedFrom":makeQuery(id+"F9.opPattern","COPY",BODY,{"derivedFrom":makeQuery(id+"F7.opRevolve","SWEPT_BODY",BODY,{"disambiguationData":[OSD([sQuery(id+"F6.wireOp",EDGE,"E7"),sQuery(id+"F6.wireOp",EDGE,"RLVqaSlf-lc0r-w3OG-rFOS-OxLLSJ0IXL9I"),sQuery(id+"F6.wireOp",EDGE,"E8"),sQuery(id+"F6.wireOp",EDGE,"E9")])]}),"instanceName":"3"}),"instanceName":"23"});
            var Q60;
            Q60=makeQuery(id+"F10.opPattern","COPY",BODY,{"derivedFrom":makeQuery(id+"F9.opPattern","COPY",BODY,{"derivedFrom":makeQuery(id+"F7.opRevolve","SWEPT_BODY",BODY,{"disambiguationData":[OSD([sQuery(id+"F6.wireOp",EDGE,"E7"),sQuery(id+"F6.wireOp",EDGE,"RLVqaSlf-lc0r-w3OG-rFOS-OxLLSJ0IXL9I"),sQuery(id+"F6.wireOp",EDGE,"E8"),sQuery(id+"F6.wireOp",EDGE,"E9")])]}),"instanceName":"1"}),"instanceName":"24"});
            var Q61;
            Q61=makeQuery(id+"F10.opPattern","COPY",BODY,{"derivedFrom":makeQuery(id+"F9.opPattern","COPY",BODY,{"derivedFrom":makeQuery(id+"F7.opRevolve","SWEPT_BODY",BODY,{"disambiguationData":[OSD([sQuery(id+"F6.wireOp",EDGE,"E7"),sQuery(id+"F6.wireOp",EDGE,"RLVqaSlf-lc0r-w3OG-rFOS-OxLLSJ0IXL9I"),sQuery(id+"F6.wireOp",EDGE,"E8"),sQuery(id+"F6.wireOp",EDGE,"E9")])]}),"instanceName":"2"}),"instanceName":"24"});
            var Q62;
            Q62=makeQuery(id+"F10.opPattern","COPY",BODY,{"derivedFrom":makeQuery(id+"F9.opPattern","COPY",BODY,{"derivedFrom":makeQuery(id+"F7.opRevolve","SWEPT_BODY",BODY,{"disambiguationData":[OSD([sQuery(id+"F6.wireOp",EDGE,"E7"),sQuery(id+"F6.wireOp",EDGE,"RLVqaSlf-lc0r-w3OG-rFOS-OxLLSJ0IXL9I"),sQuery(id+"F6.wireOp",EDGE,"E8"),sQuery(id+"F6.wireOp",EDGE,"E9")])]}),"instanceName":"3"}),"instanceName":"24"});
            var Q63;
            Q63=makeQuery(id+"F10.opPattern","COPY",BODY,{"derivedFrom":makeQuery(id+"F9.opPattern","COPY",BODY,{"derivedFrom":makeQuery(id+"F7.opRevolve","SWEPT_BODY",BODY,{"disambiguationData":[OSD([sQuery(id+"F6.wireOp",EDGE,"E7"),sQuery(id+"F6.wireOp",EDGE,"RLVqaSlf-lc0r-w3OG-rFOS-OxLLSJ0IXL9I"),sQuery(id+"F6.wireOp",EDGE,"E8"),sQuery(id+"F6.wireOp",EDGE,"E9")])]}),"instanceName":"1"}),"instanceName":"25"});
            var Q64;
            Q64=makeQuery(id+"F10.opPattern","COPY",BODY,{"derivedFrom":makeQuery(id+"F9.opPattern","COPY",BODY,{"derivedFrom":makeQuery(id+"F7.opRevolve","SWEPT_BODY",BODY,{"disambiguationData":[OSD([sQuery(id+"F6.wireOp",EDGE,"E7"),sQuery(id+"F6.wireOp",EDGE,"RLVqaSlf-lc0r-w3OG-rFOS-OxLLSJ0IXL9I"),sQuery(id+"F6.wireOp",EDGE,"E8"),sQuery(id+"F6.wireOp",EDGE,"E9")])]}),"instanceName":"2"}),"instanceName":"25"});
            var Q65;
            Q65=makeQuery(id+"F10.opPattern","COPY",BODY,{"derivedFrom":makeQuery(id+"F9.opPattern","COPY",BODY,{"derivedFrom":makeQuery(id+"F7.opRevolve","SWEPT_BODY",BODY,{"disambiguationData":[OSD([sQuery(id+"F6.wireOp",EDGE,"E7"),sQuery(id+"F6.wireOp",EDGE,"RLVqaSlf-lc0r-w3OG-rFOS-OxLLSJ0IXL9I"),sQuery(id+"F6.wireOp",EDGE,"E8"),sQuery(id+"F6.wireOp",EDGE,"E9")])]}),"instanceName":"2"}),"instanceName":"27"});
            var Q66;
            Q66=makeQuery(id+"F10.opPattern","COPY",BODY,{"derivedFrom":makeQuery(id+"F9.opPattern","COPY",BODY,{"derivedFrom":makeQuery(id+"F7.opRevolve","SWEPT_BODY",BODY,{"disambiguationData":[OSD([sQuery(id+"F6.wireOp",EDGE,"E7"),sQuery(id+"F6.wireOp",EDGE,"RLVqaSlf-lc0r-w3OG-rFOS-OxLLSJ0IXL9I"),sQuery(id+"F6.wireOp",EDGE,"E8"),sQuery(id+"F6.wireOp",EDGE,"E9")])]}),"instanceName":"1"}),"instanceName":"27"});
            var Q67;
            Q67=makeQuery(id+"F10.opPattern","COPY",BODY,{"derivedFrom":makeQuery(id+"F7.opRevolve","SWEPT_BODY",BODY,{"disambiguationData":[OSD([sQuery(id+"F6.wireOp",EDGE,"E7"),sQuery(id+"F6.wireOp",EDGE,"RLVqaSlf-lc0r-w3OG-rFOS-OxLLSJ0IXL9I"),sQuery(id+"F6.wireOp",EDGE,"E8"),sQuery(id+"F6.wireOp",EDGE,"E9")])]}),"instanceName":"27"});
            var Q68;
            Q68=makeQuery(id+"F10.opPattern","COPY",BODY,{"derivedFrom":makeQuery(id+"F9.opPattern","COPY",BODY,{"derivedFrom":makeQuery(id+"F7.opRevolve","SWEPT_BODY",BODY,{"disambiguationData":[OSD([sQuery(id+"F6.wireOp",EDGE,"E7"),sQuery(id+"F6.wireOp",EDGE,"RLVqaSlf-lc0r-w3OG-rFOS-OxLLSJ0IXL9I"),sQuery(id+"F6.wireOp",EDGE,"E8"),sQuery(id+"F6.wireOp",EDGE,"E9")])]}),"instanceName":"3"}),"instanceName":"26"});
            var Q69;
            Q69=makeQuery(id+"F10.opPattern","COPY",BODY,{"derivedFrom":makeQuery(id+"F9.opPattern","COPY",BODY,{"derivedFrom":makeQuery(id+"F7.opRevolve","SWEPT_BODY",BODY,{"disambiguationData":[OSD([sQuery(id+"F6.wireOp",EDGE,"E7"),sQuery(id+"F6.wireOp",EDGE,"RLVqaSlf-lc0r-w3OG-rFOS-OxLLSJ0IXL9I"),sQuery(id+"F6.wireOp",EDGE,"E8"),sQuery(id+"F6.wireOp",EDGE,"E9")])]}),"instanceName":"2"}),"instanceName":"26"});
            var Q70;
            Q70=makeQuery(id+"F10.opPattern","COPY",BODY,{"derivedFrom":makeQuery(id+"F9.opPattern","COPY",BODY,{"derivedFrom":makeQuery(id+"F7.opRevolve","SWEPT_BODY",BODY,{"disambiguationData":[OSD([sQuery(id+"F6.wireOp",EDGE,"E7"),sQuery(id+"F6.wireOp",EDGE,"RLVqaSlf-lc0r-w3OG-rFOS-OxLLSJ0IXL9I"),sQuery(id+"F6.wireOp",EDGE,"E8"),sQuery(id+"F6.wireOp",EDGE,"E9")])]}),"instanceName":"1"}),"instanceName":"26"});
            var Q71;
            Q71=makeQuery(id+"F10.opPattern","COPY",BODY,{"derivedFrom":makeQuery(id+"F7.opRevolve","SWEPT_BODY",BODY,{"disambiguationData":[OSD([sQuery(id+"F6.wireOp",EDGE,"E7"),sQuery(id+"F6.wireOp",EDGE,"RLVqaSlf-lc0r-w3OG-rFOS-OxLLSJ0IXL9I"),sQuery(id+"F6.wireOp",EDGE,"E8"),sQuery(id+"F6.wireOp",EDGE,"E9")])]}),"instanceName":"26"});
            var Q72;
            Q72=makeQuery(id+"F10.opPattern","COPY",BODY,{"derivedFrom":makeQuery(id+"F9.opPattern","COPY",BODY,{"derivedFrom":makeQuery(id+"F7.opRevolve","SWEPT_BODY",BODY,{"disambiguationData":[OSD([sQuery(id+"F6.wireOp",EDGE,"E7"),sQuery(id+"F6.wireOp",EDGE,"RLVqaSlf-lc0r-w3OG-rFOS-OxLLSJ0IXL9I"),sQuery(id+"F6.wireOp",EDGE,"E8"),sQuery(id+"F6.wireOp",EDGE,"E9")])]}),"instanceName":"3"}),"instanceName":"25"});
            var Q73;
            Q73=makeQuery(id+"F10.opPattern","COPY",BODY,{"derivedFrom":makeQuery(id+"F9.opPattern","COPY",BODY,{"derivedFrom":makeQuery(id+"F7.opRevolve","SWEPT_BODY",BODY,{"disambiguationData":[OSD([sQuery(id+"F6.wireOp",EDGE,"E7"),sQuery(id+"F6.wireOp",EDGE,"RLVqaSlf-lc0r-w3OG-rFOS-OxLLSJ0IXL9I"),sQuery(id+"F6.wireOp",EDGE,"E8"),sQuery(id+"F6.wireOp",EDGE,"E9")])]}),"instanceName":"3"}),"instanceName":"27"});
            var Q74;
            Q74=makeQuery(id+"F10.opPattern","COPY",BODY,{"derivedFrom":makeQuery(id+"F7.opRevolve","SWEPT_BODY",BODY,{"disambiguationData":[OSD([sQuery(id+"F6.wireOp",EDGE,"E7"),sQuery(id+"F6.wireOp",EDGE,"RLVqaSlf-lc0r-w3OG-rFOS-OxLLSJ0IXL9I"),sQuery(id+"F6.wireOp",EDGE,"E8"),sQuery(id+"F6.wireOp",EDGE,"E9")])]}),"instanceName":"28"});
            var Q75;
            Q75=makeQuery(id+"F10.opPattern","COPY",BODY,{"derivedFrom":makeQuery(id+"F9.opPattern","COPY",BODY,{"derivedFrom":makeQuery(id+"F7.opRevolve","SWEPT_BODY",BODY,{"disambiguationData":[OSD([sQuery(id+"F6.wireOp",EDGE,"E7"),sQuery(id+"F6.wireOp",EDGE,"RLVqaSlf-lc0r-w3OG-rFOS-OxLLSJ0IXL9I"),sQuery(id+"F6.wireOp",EDGE,"E8"),sQuery(id+"F6.wireOp",EDGE,"E9")])]}),"instanceName":"1"}),"instanceName":"28"});
            var Q76;
            Q76=makeQuery(id+"F10.opPattern","COPY",BODY,{"derivedFrom":makeQuery(id+"F9.opPattern","COPY",BODY,{"derivedFrom":makeQuery(id+"F7.opRevolve","SWEPT_BODY",BODY,{"disambiguationData":[OSD([sQuery(id+"F6.wireOp",EDGE,"E7"),sQuery(id+"F6.wireOp",EDGE,"RLVqaSlf-lc0r-w3OG-rFOS-OxLLSJ0IXL9I"),sQuery(id+"F6.wireOp",EDGE,"E8"),sQuery(id+"F6.wireOp",EDGE,"E9")])]}),"instanceName":"2"}),"instanceName":"28"});
            var Q77;
            Q77=makeQuery(id+"F10.opPattern","COPY",BODY,{"derivedFrom":makeQuery(id+"F9.opPattern","COPY",BODY,{"derivedFrom":makeQuery(id+"F7.opRevolve","SWEPT_BODY",BODY,{"disambiguationData":[OSD([sQuery(id+"F6.wireOp",EDGE,"E7"),sQuery(id+"F6.wireOp",EDGE,"RLVqaSlf-lc0r-w3OG-rFOS-OxLLSJ0IXL9I"),sQuery(id+"F6.wireOp",EDGE,"E8"),sQuery(id+"F6.wireOp",EDGE,"E9")])]}),"instanceName":"3"}),"instanceName":"28"});
            var Q78;
            Q78=makeQuery(id+"F10.opPattern","COPY",BODY,{"derivedFrom":makeQuery(id+"F7.opRevolve","SWEPT_BODY",BODY,{"disambiguationData":[OSD([sQuery(id+"F6.wireOp",EDGE,"E7"),sQuery(id+"F6.wireOp",EDGE,"RLVqaSlf-lc0r-w3OG-rFOS-OxLLSJ0IXL9I"),sQuery(id+"F6.wireOp",EDGE,"E8"),sQuery(id+"F6.wireOp",EDGE,"E9")])]}),"instanceName":"29"});
            var Q79;
            Q79=makeQuery(id+"F10.opPattern","COPY",BODY,{"derivedFrom":makeQuery(id+"F9.opPattern","COPY",BODY,{"derivedFrom":makeQuery(id+"F7.opRevolve","SWEPT_BODY",BODY,{"disambiguationData":[OSD([sQuery(id+"F6.wireOp",EDGE,"E7"),sQuery(id+"F6.wireOp",EDGE,"RLVqaSlf-lc0r-w3OG-rFOS-OxLLSJ0IXL9I"),sQuery(id+"F6.wireOp",EDGE,"E8"),sQuery(id+"F6.wireOp",EDGE,"E9")])]}),"instanceName":"3"}),"instanceName":"1"});
            var Q80;
            Q80=makeQuery(id+"F10.opPattern","COPY",BODY,{"derivedFrom":makeQuery(id+"F9.opPattern","COPY",BODY,{"derivedFrom":makeQuery(id+"F7.opRevolve","SWEPT_BODY",BODY,{"disambiguationData":[OSD([sQuery(id+"F6.wireOp",EDGE,"E7"),sQuery(id+"F6.wireOp",EDGE,"RLVqaSlf-lc0r-w3OG-rFOS-OxLLSJ0IXL9I"),sQuery(id+"F6.wireOp",EDGE,"E8"),sQuery(id+"F6.wireOp",EDGE,"E9")])]}),"instanceName":"2"}),"instanceName":"29"});
            var Q81;
            Q81=makeQuery(id+"F10.opPattern","COPY",BODY,{"derivedFrom":makeQuery(id+"F9.opPattern","COPY",BODY,{"derivedFrom":makeQuery(id+"F7.opRevolve","SWEPT_BODY",BODY,{"disambiguationData":[OSD([sQuery(id+"F6.wireOp",EDGE,"E7"),sQuery(id+"F6.wireOp",EDGE,"RLVqaSlf-lc0r-w3OG-rFOS-OxLLSJ0IXL9I"),sQuery(id+"F6.wireOp",EDGE,"E8"),sQuery(id+"F6.wireOp",EDGE,"E9")])]}),"instanceName":"1"}),"instanceName":"29"});
            var Q82;
            Q82=makeQuery(id+"F10.opPattern","COPY",BODY,{"derivedFrom":makeQuery(id+"F9.opPattern","COPY",BODY,{"derivedFrom":makeQuery(id+"F7.opRevolve","SWEPT_BODY",BODY,{"disambiguationData":[OSD([sQuery(id+"F6.wireOp",EDGE,"E7"),sQuery(id+"F6.wireOp",EDGE,"RLVqaSlf-lc0r-w3OG-rFOS-OxLLSJ0IXL9I"),sQuery(id+"F6.wireOp",EDGE,"E8"),sQuery(id+"F6.wireOp",EDGE,"E9")])]}),"instanceName":"3"}),"instanceName":"29"});
            var Q83;
            Q83=makeQuery(id+"F7.opRevolve","SWEPT_BODY",BODY,{"disambiguationData":[OSD([sQuery(id+"F6.wireOp",EDGE,"E7"),sQuery(id+"F6.wireOp",EDGE,"RLVqaSlf-lc0r-w3OG-rFOS-OxLLSJ0IXL9I"),sQuery(id+"F6.wireOp",EDGE,"E8"),sQuery(id+"F6.wireOp",EDGE,"E9")])]});
            var Q84;
            Q84=makeQuery(id+"F10.opPattern","COPY",BODY,{"derivedFrom":makeQuery(id+"F7.opRevolve","SWEPT_BODY",BODY,{"disambiguationData":[OSD([sQuery(id+"F6.wireOp",EDGE,"E7"),sQuery(id+"F6.wireOp",EDGE,"RLVqaSlf-lc0r-w3OG-rFOS-OxLLSJ0IXL9I"),sQuery(id+"F6.wireOp",EDGE,"E8"),sQuery(id+"F6.wireOp",EDGE,"E9")])]}),"instanceName":"2"});
            var Q85;
            Q85=makeQuery(id+"F10.opPattern","COPY",BODY,{"derivedFrom":makeQuery(id+"F7.opRevolve","SWEPT_BODY",BODY,{"disambiguationData":[OSD([sQuery(id+"F6.wireOp",EDGE,"E7"),sQuery(id+"F6.wireOp",EDGE,"RLVqaSlf-lc0r-w3OG-rFOS-OxLLSJ0IXL9I"),sQuery(id+"F6.wireOp",EDGE,"E8"),sQuery(id+"F6.wireOp",EDGE,"E9")])]}),"instanceName":"7"});
            var Q86;
            Q86=makeQuery(id+"F10.opPattern","COPY",BODY,{"derivedFrom":makeQuery(id+"F7.opRevolve","SWEPT_BODY",BODY,{"disambiguationData":[OSD([sQuery(id+"F6.wireOp",EDGE,"E7"),sQuery(id+"F6.wireOp",EDGE,"RLVqaSlf-lc0r-w3OG-rFOS-OxLLSJ0IXL9I"),sQuery(id+"F6.wireOp",EDGE,"E8"),sQuery(id+"F6.wireOp",EDGE,"E9")])]}),"instanceName":"8"});
            var Q87;
            Q87=makeQuery(id+"F10.opPattern","COPY",BODY,{"derivedFrom":makeQuery(id+"F7.opRevolve","SWEPT_BODY",BODY,{"disambiguationData":[OSD([sQuery(id+"F6.wireOp",EDGE,"E7"),sQuery(id+"F6.wireOp",EDGE,"RLVqaSlf-lc0r-w3OG-rFOS-OxLLSJ0IXL9I"),sQuery(id+"F6.wireOp",EDGE,"E8"),sQuery(id+"F6.wireOp",EDGE,"E9")])]}),"instanceName":"9"});
            var Q88;
            Q88=makeQuery(id+"F10.opPattern","COPY",BODY,{"derivedFrom":makeQuery(id+"F7.opRevolve","SWEPT_BODY",BODY,{"disambiguationData":[OSD([sQuery(id+"F6.wireOp",EDGE,"E7"),sQuery(id+"F6.wireOp",EDGE,"RLVqaSlf-lc0r-w3OG-rFOS-OxLLSJ0IXL9I"),sQuery(id+"F6.wireOp",EDGE,"E8"),sQuery(id+"F6.wireOp",EDGE,"E9")])]}),"instanceName":"10"});
            var Q89;
            Q89=makeQuery(id+"F10.opPattern","COPY",BODY,{"derivedFrom":makeQuery(id+"F7.opRevolve","SWEPT_BODY",BODY,{"disambiguationData":[OSD([sQuery(id+"F6.wireOp",EDGE,"E7"),sQuery(id+"F6.wireOp",EDGE,"RLVqaSlf-lc0r-w3OG-rFOS-OxLLSJ0IXL9I"),sQuery(id+"F6.wireOp",EDGE,"E8"),sQuery(id+"F6.wireOp",EDGE,"E9")])]}),"instanceName":"11"});
            var Q90;
            Q90=makeQuery(id+"F10.opPattern","COPY",BODY,{"derivedFrom":makeQuery(id+"F7.opRevolve","SWEPT_BODY",BODY,{"disambiguationData":[OSD([sQuery(id+"F6.wireOp",EDGE,"E7"),sQuery(id+"F6.wireOp",EDGE,"RLVqaSlf-lc0r-w3OG-rFOS-OxLLSJ0IXL9I"),sQuery(id+"F6.wireOp",EDGE,"E8"),sQuery(id+"F6.wireOp",EDGE,"E9")])]}),"instanceName":"12"});
            var Q91;
            Q91=makeQuery(id+"F10.opPattern","COPY",BODY,{"derivedFrom":makeQuery(id+"F9.opPattern","COPY",BODY,{"derivedFrom":makeQuery(id+"F7.opRevolve","SWEPT_BODY",BODY,{"disambiguationData":[OSD([sQuery(id+"F6.wireOp",EDGE,"E7"),sQuery(id+"F6.wireOp",EDGE,"RLVqaSlf-lc0r-w3OG-rFOS-OxLLSJ0IXL9I"),sQuery(id+"F6.wireOp",EDGE,"E8"),sQuery(id+"F6.wireOp",EDGE,"E9")])]}),"instanceName":"1"}),"instanceName":"12"});
            var Q92;
            Q92=makeQuery(id+"F10.opPattern","COPY",BODY,{"derivedFrom":makeQuery(id+"F9.opPattern","COPY",BODY,{"derivedFrom":makeQuery(id+"F7.opRevolve","SWEPT_BODY",BODY,{"disambiguationData":[OSD([sQuery(id+"F6.wireOp",EDGE,"E7"),sQuery(id+"F6.wireOp",EDGE,"RLVqaSlf-lc0r-w3OG-rFOS-OxLLSJ0IXL9I"),sQuery(id+"F6.wireOp",EDGE,"E8"),sQuery(id+"F6.wireOp",EDGE,"E9")])]}),"instanceName":"2"}),"instanceName":"12"});
            var Q93;
            Q93=makeQuery(id+"F10.opPattern","COPY",BODY,{"derivedFrom":makeQuery(id+"F7.opRevolve","SWEPT_BODY",BODY,{"disambiguationData":[OSD([sQuery(id+"F6.wireOp",EDGE,"E7"),sQuery(id+"F6.wireOp",EDGE,"RLVqaSlf-lc0r-w3OG-rFOS-OxLLSJ0IXL9I"),sQuery(id+"F6.wireOp",EDGE,"E8"),sQuery(id+"F6.wireOp",EDGE,"E9")])]}),"instanceName":"13"});
            var Q94;
            Q94=makeQuery(id+"F10.opPattern","COPY",BODY,{"derivedFrom":makeQuery(id+"F9.opPattern","COPY",BODY,{"derivedFrom":makeQuery(id+"F7.opRevolve","SWEPT_BODY",BODY,{"disambiguationData":[OSD([sQuery(id+"F6.wireOp",EDGE,"E7"),sQuery(id+"F6.wireOp",EDGE,"RLVqaSlf-lc0r-w3OG-rFOS-OxLLSJ0IXL9I"),sQuery(id+"F6.wireOp",EDGE,"E8"),sQuery(id+"F6.wireOp",EDGE,"E9")])]}),"instanceName":"1"}),"instanceName":"13"});
            var Q95;
            Q95=makeQuery(id+"F10.opPattern","COPY",BODY,{"derivedFrom":makeQuery(id+"F9.opPattern","COPY",BODY,{"derivedFrom":makeQuery(id+"F7.opRevolve","SWEPT_BODY",BODY,{"disambiguationData":[OSD([sQuery(id+"F6.wireOp",EDGE,"E7"),sQuery(id+"F6.wireOp",EDGE,"RLVqaSlf-lc0r-w3OG-rFOS-OxLLSJ0IXL9I"),sQuery(id+"F6.wireOp",EDGE,"E8"),sQuery(id+"F6.wireOp",EDGE,"E9")])]}),"instanceName":"2"}),"instanceName":"13"});
            var Q96;
            Q96=makeQuery(id+"F10.opPattern","COPY",BODY,{"derivedFrom":makeQuery(id+"F7.opRevolve","SWEPT_BODY",BODY,{"disambiguationData":[OSD([sQuery(id+"F6.wireOp",EDGE,"E7"),sQuery(id+"F6.wireOp",EDGE,"RLVqaSlf-lc0r-w3OG-rFOS-OxLLSJ0IXL9I"),sQuery(id+"F6.wireOp",EDGE,"E8"),sQuery(id+"F6.wireOp",EDGE,"E9")])]}),"instanceName":"14"});
            var Q97;
            Q97=makeQuery(id+"F10.opPattern","COPY",BODY,{"derivedFrom":makeQuery(id+"F9.opPattern","COPY",BODY,{"derivedFrom":makeQuery(id+"F7.opRevolve","SWEPT_BODY",BODY,{"disambiguationData":[OSD([sQuery(id+"F6.wireOp",EDGE,"E7"),sQuery(id+"F6.wireOp",EDGE,"RLVqaSlf-lc0r-w3OG-rFOS-OxLLSJ0IXL9I"),sQuery(id+"F6.wireOp",EDGE,"E8"),sQuery(id+"F6.wireOp",EDGE,"E9")])]}),"instanceName":"1"}),"instanceName":"14"});
            var Q98;
            Q98=makeQuery(id+"F10.opPattern","COPY",BODY,{"derivedFrom":makeQuery(id+"F9.opPattern","COPY",BODY,{"derivedFrom":makeQuery(id+"F7.opRevolve","SWEPT_BODY",BODY,{"disambiguationData":[OSD([sQuery(id+"F6.wireOp",EDGE,"E7"),sQuery(id+"F6.wireOp",EDGE,"RLVqaSlf-lc0r-w3OG-rFOS-OxLLSJ0IXL9I"),sQuery(id+"F6.wireOp",EDGE,"E8"),sQuery(id+"F6.wireOp",EDGE,"E9")])]}),"instanceName":"2"}),"instanceName":"14"});
            var Q99;
            Q99=makeQuery(id+"F10.opPattern","COPY",BODY,{"derivedFrom":makeQuery(id+"F7.opRevolve","SWEPT_BODY",BODY,{"disambiguationData":[OSD([sQuery(id+"F6.wireOp",EDGE,"E7"),sQuery(id+"F6.wireOp",EDGE,"RLVqaSlf-lc0r-w3OG-rFOS-OxLLSJ0IXL9I"),sQuery(id+"F6.wireOp",EDGE,"E8"),sQuery(id+"F6.wireOp",EDGE,"E9")])]}),"instanceName":"15"});
            var Q100;
            Q100=makeQuery(id+"F10.opPattern","COPY",BODY,{"derivedFrom":makeQuery(id+"F9.opPattern","COPY",BODY,{"derivedFrom":makeQuery(id+"F7.opRevolve","SWEPT_BODY",BODY,{"disambiguationData":[OSD([sQuery(id+"F6.wireOp",EDGE,"E7"),sQuery(id+"F6.wireOp",EDGE,"RLVqaSlf-lc0r-w3OG-rFOS-OxLLSJ0IXL9I"),sQuery(id+"F6.wireOp",EDGE,"E8"),sQuery(id+"F6.wireOp",EDGE,"E9")])]}),"instanceName":"1"}),"instanceName":"15"});
            var Q101;
            Q101=makeQuery(id+"F10.opPattern","COPY",BODY,{"derivedFrom":makeQuery(id+"F9.opPattern","COPY",BODY,{"derivedFrom":makeQuery(id+"F7.opRevolve","SWEPT_BODY",BODY,{"disambiguationData":[OSD([sQuery(id+"F6.wireOp",EDGE,"E7"),sQuery(id+"F6.wireOp",EDGE,"RLVqaSlf-lc0r-w3OG-rFOS-OxLLSJ0IXL9I"),sQuery(id+"F6.wireOp",EDGE,"E8"),sQuery(id+"F6.wireOp",EDGE,"E9")])]}),"instanceName":"2"}),"instanceName":"15"});
            var Q102;
            Q102=makeQuery(id+"F10.opPattern","COPY",BODY,{"derivedFrom":makeQuery(id+"F7.opRevolve","SWEPT_BODY",BODY,{"disambiguationData":[OSD([sQuery(id+"F6.wireOp",EDGE,"E7"),sQuery(id+"F6.wireOp",EDGE,"RLVqaSlf-lc0r-w3OG-rFOS-OxLLSJ0IXL9I"),sQuery(id+"F6.wireOp",EDGE,"E8"),sQuery(id+"F6.wireOp",EDGE,"E9")])]}),"instanceName":"16"});
            var Q103;
            Q103=makeQuery(id+"F10.opPattern","COPY",BODY,{"derivedFrom":makeQuery(id+"F9.opPattern","COPY",BODY,{"derivedFrom":makeQuery(id+"F7.opRevolve","SWEPT_BODY",BODY,{"disambiguationData":[OSD([sQuery(id+"F6.wireOp",EDGE,"E7"),sQuery(id+"F6.wireOp",EDGE,"RLVqaSlf-lc0r-w3OG-rFOS-OxLLSJ0IXL9I"),sQuery(id+"F6.wireOp",EDGE,"E8"),sQuery(id+"F6.wireOp",EDGE,"E9")])]}),"instanceName":"1"}),"instanceName":"16"});
            var Q104;
            Q104=makeQuery(id+"F10.opPattern","COPY",BODY,{"derivedFrom":makeQuery(id+"F9.opPattern","COPY",BODY,{"derivedFrom":makeQuery(id+"F7.opRevolve","SWEPT_BODY",BODY,{"disambiguationData":[OSD([sQuery(id+"F6.wireOp",EDGE,"E7"),sQuery(id+"F6.wireOp",EDGE,"RLVqaSlf-lc0r-w3OG-rFOS-OxLLSJ0IXL9I"),sQuery(id+"F6.wireOp",EDGE,"E8"),sQuery(id+"F6.wireOp",EDGE,"E9")])]}),"instanceName":"2"}),"instanceName":"16"});
            var Q105;
            Q105=makeQuery(id+"F10.opPattern","COPY",BODY,{"derivedFrom":makeQuery(id+"F7.opRevolve","SWEPT_BODY",BODY,{"disambiguationData":[OSD([sQuery(id+"F6.wireOp",EDGE,"E7"),sQuery(id+"F6.wireOp",EDGE,"RLVqaSlf-lc0r-w3OG-rFOS-OxLLSJ0IXL9I"),sQuery(id+"F6.wireOp",EDGE,"E8"),sQuery(id+"F6.wireOp",EDGE,"E9")])]}),"instanceName":"17"});
            var Q106;
            Q106=makeQuery(id+"F10.opPattern","COPY",BODY,{"derivedFrom":makeQuery(id+"F9.opPattern","COPY",BODY,{"derivedFrom":makeQuery(id+"F7.opRevolve","SWEPT_BODY",BODY,{"disambiguationData":[OSD([sQuery(id+"F6.wireOp",EDGE,"E7"),sQuery(id+"F6.wireOp",EDGE,"RLVqaSlf-lc0r-w3OG-rFOS-OxLLSJ0IXL9I"),sQuery(id+"F6.wireOp",EDGE,"E8"),sQuery(id+"F6.wireOp",EDGE,"E9")])]}),"instanceName":"2"}),"instanceName":"17"});
            var Q107;
            Q107=makeQuery(id+"F10.opPattern","COPY",BODY,{"derivedFrom":makeQuery(id+"F7.opRevolve","SWEPT_BODY",BODY,{"disambiguationData":[OSD([sQuery(id+"F6.wireOp",EDGE,"E7"),sQuery(id+"F6.wireOp",EDGE,"RLVqaSlf-lc0r-w3OG-rFOS-OxLLSJ0IXL9I"),sQuery(id+"F6.wireOp",EDGE,"E8"),sQuery(id+"F6.wireOp",EDGE,"E9")])]}),"instanceName":"18"});
            var Q108;
            Q108=makeQuery(id+"F10.opPattern","COPY",BODY,{"derivedFrom":makeQuery(id+"F9.opPattern","COPY",BODY,{"derivedFrom":makeQuery(id+"F7.opRevolve","SWEPT_BODY",BODY,{"disambiguationData":[OSD([sQuery(id+"F6.wireOp",EDGE,"E7"),sQuery(id+"F6.wireOp",EDGE,"RLVqaSlf-lc0r-w3OG-rFOS-OxLLSJ0IXL9I"),sQuery(id+"F6.wireOp",EDGE,"E8"),sQuery(id+"F6.wireOp",EDGE,"E9")])]}),"instanceName":"2"}),"instanceName":"18"});
            var Q109;
            Q109=makeQuery(id+"F10.opPattern","COPY",BODY,{"derivedFrom":makeQuery(id+"F7.opRevolve","SWEPT_BODY",BODY,{"disambiguationData":[OSD([sQuery(id+"F6.wireOp",EDGE,"E7"),sQuery(id+"F6.wireOp",EDGE,"RLVqaSlf-lc0r-w3OG-rFOS-OxLLSJ0IXL9I"),sQuery(id+"F6.wireOp",EDGE,"E8"),sQuery(id+"F6.wireOp",EDGE,"E9")])]}),"instanceName":"19"});
            var Q110;
            Q110=makeQuery(id+"F10.opPattern","COPY",BODY,{"derivedFrom":makeQuery(id+"F9.opPattern","COPY",BODY,{"derivedFrom":makeQuery(id+"F7.opRevolve","SWEPT_BODY",BODY,{"disambiguationData":[OSD([sQuery(id+"F6.wireOp",EDGE,"E7"),sQuery(id+"F6.wireOp",EDGE,"RLVqaSlf-lc0r-w3OG-rFOS-OxLLSJ0IXL9I"),sQuery(id+"F6.wireOp",EDGE,"E8"),sQuery(id+"F6.wireOp",EDGE,"E9")])]}),"instanceName":"1"}),"instanceName":"19"});
            var Q111;
            Q111=makeQuery(id+"F10.opPattern","COPY",BODY,{"derivedFrom":makeQuery(id+"F7.opRevolve","SWEPT_BODY",BODY,{"disambiguationData":[OSD([sQuery(id+"F6.wireOp",EDGE,"E7"),sQuery(id+"F6.wireOp",EDGE,"RLVqaSlf-lc0r-w3OG-rFOS-OxLLSJ0IXL9I"),sQuery(id+"F6.wireOp",EDGE,"E8"),sQuery(id+"F6.wireOp",EDGE,"E9")])]}),"instanceName":"20"});
            var Q112;
            Q112=makeQuery(id+"F10.opPattern","COPY",BODY,{"derivedFrom":makeQuery(id+"F9.opPattern","COPY",BODY,{"derivedFrom":makeQuery(id+"F7.opRevolve","SWEPT_BODY",BODY,{"disambiguationData":[OSD([sQuery(id+"F6.wireOp",EDGE,"E7"),sQuery(id+"F6.wireOp",EDGE,"RLVqaSlf-lc0r-w3OG-rFOS-OxLLSJ0IXL9I"),sQuery(id+"F6.wireOp",EDGE,"E8"),sQuery(id+"F6.wireOp",EDGE,"E9")])]}),"instanceName":"1"}),"instanceName":"20"});
            var Q113;
            Q113=makeQuery(id+"F10.opPattern","COPY",BODY,{"derivedFrom":makeQuery(id+"F7.opRevolve","SWEPT_BODY",BODY,{"disambiguationData":[OSD([sQuery(id+"F6.wireOp",EDGE,"E7"),sQuery(id+"F6.wireOp",EDGE,"RLVqaSlf-lc0r-w3OG-rFOS-OxLLSJ0IXL9I"),sQuery(id+"F6.wireOp",EDGE,"E8"),sQuery(id+"F6.wireOp",EDGE,"E9")])]}),"instanceName":"21"});
            var Q114;
            Q114=makeQuery(id+"F10.opPattern","COPY",BODY,{"derivedFrom":makeQuery(id+"F7.opRevolve","SWEPT_BODY",BODY,{"disambiguationData":[OSD([sQuery(id+"F6.wireOp",EDGE,"E7"),sQuery(id+"F6.wireOp",EDGE,"RLVqaSlf-lc0r-w3OG-rFOS-OxLLSJ0IXL9I"),sQuery(id+"F6.wireOp",EDGE,"E8"),sQuery(id+"F6.wireOp",EDGE,"E9")])]}),"instanceName":"22"});
            var Q115;
            Q115=makeQuery(id+"F10.opPattern","COPY",BODY,{"derivedFrom":makeQuery(id+"F7.opRevolve","SWEPT_BODY",BODY,{"disambiguationData":[OSD([sQuery(id+"F6.wireOp",EDGE,"E7"),sQuery(id+"F6.wireOp",EDGE,"RLVqaSlf-lc0r-w3OG-rFOS-OxLLSJ0IXL9I"),sQuery(id+"F6.wireOp",EDGE,"E8"),sQuery(id+"F6.wireOp",EDGE,"E9")])]}),"instanceName":"23"});
            var Q116;
            Q116=makeQuery(id+"F10.opPattern","COPY",BODY,{"derivedFrom":makeQuery(id+"F7.opRevolve","SWEPT_BODY",BODY,{"disambiguationData":[OSD([sQuery(id+"F6.wireOp",EDGE,"E7"),sQuery(id+"F6.wireOp",EDGE,"RLVqaSlf-lc0r-w3OG-rFOS-OxLLSJ0IXL9I"),sQuery(id+"F6.wireOp",EDGE,"E8"),sQuery(id+"F6.wireOp",EDGE,"E9")])]}),"instanceName":"24"});
            var Q117;
            Q117=makeQuery(id+"F10.opPattern","COPY",BODY,{"derivedFrom":makeQuery(id+"F7.opRevolve","SWEPT_BODY",BODY,{"disambiguationData":[OSD([sQuery(id+"F6.wireOp",EDGE,"E7"),sQuery(id+"F6.wireOp",EDGE,"RLVqaSlf-lc0r-w3OG-rFOS-OxLLSJ0IXL9I"),sQuery(id+"F6.wireOp",EDGE,"E8"),sQuery(id+"F6.wireOp",EDGE,"E9")])]}),"instanceName":"25"});
            var Q118;
            Q118=makeQuery(id+"F10.opPattern","COPY",BODY,{"derivedFrom":makeQuery(id+"F9.opPattern","COPY",BODY,{"derivedFrom":makeQuery(id+"F7.opRevolve","SWEPT_BODY",BODY,{"disambiguationData":[OSD([sQuery(id+"F6.wireOp",EDGE,"E7"),sQuery(id+"F6.wireOp",EDGE,"RLVqaSlf-lc0r-w3OG-rFOS-OxLLSJ0IXL9I"),sQuery(id+"F6.wireOp",EDGE,"E8"),sQuery(id+"F6.wireOp",EDGE,"E9")])]}),"instanceName":"1"}),"instanceName":"17"});
            var Q119;
            Q119=makeQuery(id+"F10.opPattern","COPY",BODY,{"derivedFrom":makeQuery(id+"F9.opPattern","COPY",BODY,{"derivedFrom":makeQuery(id+"F7.opRevolve","SWEPT_BODY",BODY,{"disambiguationData":[OSD([sQuery(id+"F6.wireOp",EDGE,"E7"),sQuery(id+"F6.wireOp",EDGE,"RLVqaSlf-lc0r-w3OG-rFOS-OxLLSJ0IXL9I"),sQuery(id+"F6.wireOp",EDGE,"E8"),sQuery(id+"F6.wireOp",EDGE,"E9")])]}),"instanceName":"1"}),"instanceName":"18"});
            var Q120;
            Q120=sQuery(id+"F11.wireOp",EDGE,"E11");
            circularPattern(context, id + "F12", {"entities" : qUnion([Q0, Q1, Q2, Q3, Q4, Q5, Q6, Q7, Q8, Q9, Q10, Q11, Q12, Q13, Q14, Q15, Q16, Q17, Q18, Q19, Q20, Q21, Q22, Q23, Q24, Q25, Q26, Q27, Q28, Q29, Q30, Q31, Q32, Q33, Q34, Q35, Q36, Q37, Q38, Q39, Q40, Q41, Q42, Q43, Q44, Q45, Q46, Q47, Q48, Q49, Q50, Q51, Q52, Q53, Q54, Q55, Q56, Q57, Q58, Q59, Q60, Q61, Q62, Q63, Q64, Q65, Q66, Q67, Q68, Q69, Q70, Q71, Q72, Q73, Q74, Q75, Q76, Q77, Q78, Q79, Q80, Q81, Q82, Q83, Q84, Q85, Q86, Q87, Q88, Q89, Q90, Q91, Q92, Q93, Q94, Q95, Q96, Q97, Q98, Q99, Q100, Q101, Q102, Q103, Q104, Q105, Q106, Q107, Q108, Q109, Q110, Q111, Q112, Q113, Q114, Q115, Q116, Q117, Q118, Q119]), "axis" : qUnion([Q120]), "angle" : 360 * degree, "instanceCount" : 3, "equalSpace" : true});
        }
        {
            var Q0;
            Q0=makeQuery(id+"F1.opExtrude","CAP_EDGE",EDGE,{"disambiguationData":[OSD([sQuery(id+"F0.wireOp",EDGE,"E3")])],"isStart":true});
            var Q1;
            Q1=makeQuery(id+"F1.opExtrude","CAP_EDGE",EDGE,{"disambiguationData":[OSD([sQuery(id+"F0.wireOp",EDGE,"E0")])],"isStart":true});
            var Q2;
            Q2=makeQuery(id+"F1.opExtrude","CAP_EDGE",EDGE,{"disambiguationData":[OSD([sQuery(id+"F0.wireOp",EDGE,"E4.1.1")])],"isStart":true});
            var Q3;
            Q3=makeQuery(id+"F1.opExtrude","CAP_EDGE",EDGE,{"disambiguationData":[OSD([sQuery(id+"F0.wireOp",EDGE,"E4.2.1")])],"isStart":true});
            var Q4;
            Q4=makeQuery(id+"F1.opExtrude","CAP_EDGE",EDGE,{"disambiguationData":[OSD([sQuery(id+"F0.wireOp",EDGE,"E4.2.1")])],"isStart":false});
            var Q5;
            Q5=makeQuery(id+"F1.opExtrude","CAP_EDGE",EDGE,{"disambiguationData":[OSD([sQuery(id+"F0.wireOp",EDGE,"E0")])],"isStart":false});
            var Q6;
            Q6=makeQuery(id+"F1.opExtrude","SWEPT_FACE",FACE,{"disambiguationData":[OSD([sQuery(id+"F0.wireOp",EDGE,"E4.1.1")])]});
            var Q7;
            Q7=makeQuery(id+"F1.opExtrude","CAP_EDGE",EDGE,{"disambiguationData":[OSD([sQuery(id+"F0.wireOp",EDGE,"E3")])],"isStart":false});
            chamfer(context, id + "F13", {"entities" : qUnion([Q0, Q1, Q2, Q3, Q4, Q5, Q6, Q7]), "width" : 0.5 * mm, "tangentPropagation" : true});
        }
    });
